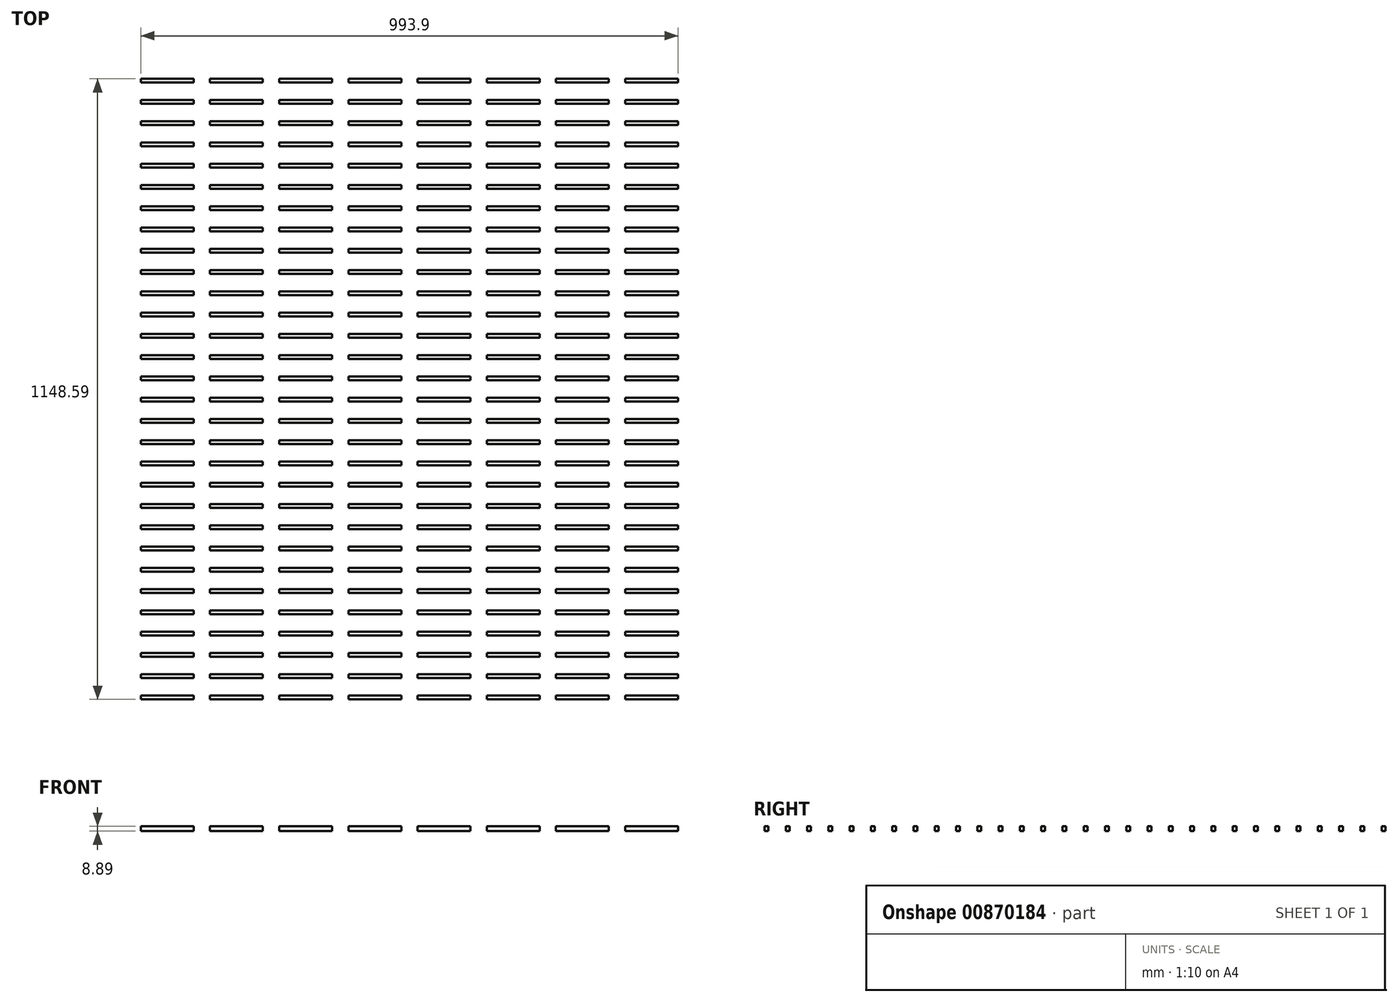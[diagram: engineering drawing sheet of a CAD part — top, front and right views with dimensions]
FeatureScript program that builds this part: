
annotation { "Feature Type Name" : "Feature", "Feature Type Description" : "" }
export const myFeature = defineFeature(function(context is Context, id is Id, definition is map)
    precondition{}
    {
        {
            var Q0;
            Q0=qCreatedBy(makeId("Top.planeOp"),FACE);
            var sketch = newSketch(context, id + "F0", { "sketchPlane" : qUnion([Q0])});
            skLineSegment(sketch, "E0.bottom", {"start": v(-104.49, 66.32) * mm, "end": v(-6.7, 66.32) * mm});
            skLineSegment(sketch, "E0.top", {"start": v(-104.49, 59.46) * mm, "end": v(-6.7, 59.46) * mm});
            skLineSegment(sketch, "E0.left", {"start": v(-104.49, 66.32) * mm, "end": v(-104.49, 59.46) * mm});
            skLineSegment(sketch, "E0.right", {"start": v(-6.7, 66.32) * mm, "end": v(-6.7, 59.46) * mm});
            skLineSegment(sketch, "E1.0.1.0", {"start": v(-104.49, 105.69) * mm, "end": v(-6.7, 105.69) * mm});
            skLineSegment(sketch, "E1.0.1.1", {"start": v(-104.49, 98.83) * mm, "end": v(-6.7, 98.83) * mm});
            skLineSegment(sketch, "E1.0.1.2", {"start": v(-6.7, 105.69) * mm, "end": v(-6.7, 98.83) * mm});
            skLineSegment(sketch, "E1.0.1.3", {"start": v(-104.49, 105.69) * mm, "end": v(-104.49, 98.83) * mm});
            skLineSegment(sketch, "E1.0.2.0", {"start": v(-104.49, 145.06) * mm, "end": v(-6.7, 145.06) * mm});
            skLineSegment(sketch, "E1.0.2.1", {"start": v(-104.49, 138.2) * mm, "end": v(-6.7, 138.2) * mm});
            skLineSegment(sketch, "E1.0.2.2", {"start": v(-6.7, 145.06) * mm, "end": v(-6.7, 138.2) * mm});
            skLineSegment(sketch, "E1.0.2.3", {"start": v(-104.49, 145.06) * mm, "end": v(-104.49, 138.2) * mm});
            skLineSegment(sketch, "E1.0.3.0", {"start": v(-104.49, 184.43) * mm, "end": v(-6.7, 184.43) * mm});
            skLineSegment(sketch, "E1.0.3.1", {"start": v(-104.49, 177.57) * mm, "end": v(-6.7, 177.57) * mm});
            skLineSegment(sketch, "E1.0.3.2", {"start": v(-6.7, 184.43) * mm, "end": v(-6.7, 177.57) * mm});
            skLineSegment(sketch, "E1.0.3.3", {"start": v(-104.49, 184.43) * mm, "end": v(-104.49, 177.57) * mm});
            skLineSegment(sketch, "E1.0.4.0", {"start": v(-104.49, 223.8) * mm, "end": v(-6.7, 223.8) * mm});
            skLineSegment(sketch, "E1.0.4.1", {"start": v(-104.49, 216.94) * mm, "end": v(-6.7, 216.94) * mm});
            skLineSegment(sketch, "E1.0.4.2", {"start": v(-6.7, 223.8) * mm, "end": v(-6.7, 216.94) * mm});
            skLineSegment(sketch, "E1.0.4.3", {"start": v(-104.49, 223.8) * mm, "end": v(-104.49, 216.94) * mm});
            skLineSegment(sketch, "E1.0.5.0", {"start": v(-104.49, 263.17) * mm, "end": v(-6.7, 263.17) * mm});
            skLineSegment(sketch, "E1.0.5.1", {"start": v(-104.49, 256.31) * mm, "end": v(-6.7, 256.31) * mm});
            skLineSegment(sketch, "E1.0.5.2", {"start": v(-6.7, 263.17) * mm, "end": v(-6.7, 256.31) * mm});
            skLineSegment(sketch, "E1.0.5.3", {"start": v(-104.49, 263.17) * mm, "end": v(-104.49, 256.31) * mm});
            skLineSegment(sketch, "E1.0.6.0", {"start": v(-104.49, 302.54) * mm, "end": v(-6.7, 302.54) * mm});
            skLineSegment(sketch, "E1.0.6.1", {"start": v(-104.49, 295.68) * mm, "end": v(-6.7, 295.68) * mm});
            skLineSegment(sketch, "E1.0.6.2", {"start": v(-6.7, 302.54) * mm, "end": v(-6.7, 295.68) * mm});
            skLineSegment(sketch, "E1.0.6.3", {"start": v(-104.49, 302.54) * mm, "end": v(-104.49, 295.68) * mm});
            skLineSegment(sketch, "E1.0.7.0", {"start": v(-104.49, 341.9) * mm, "end": v(-6.7, 341.9) * mm});
            skLineSegment(sketch, "E1.0.7.1", {"start": v(-104.49, 335.05) * mm, "end": v(-6.7, 335.05) * mm});
            skLineSegment(sketch, "E1.0.7.2", {"start": v(-6.7, 341.9) * mm, "end": v(-6.7, 335.05) * mm});
            skLineSegment(sketch, "E1.0.7.3", {"start": v(-104.49, 341.9) * mm, "end": v(-104.49, 335.05) * mm});
            skLineSegment(sketch, "E1.0.8.0", {"start": v(-104.49, 381.28) * mm, "end": v(-6.7, 381.28) * mm});
            skLineSegment(sketch, "E1.0.8.1", {"start": v(-104.49, 374.42) * mm, "end": v(-6.7, 374.42) * mm});
            skLineSegment(sketch, "E1.0.8.2", {"start": v(-6.7, 381.28) * mm, "end": v(-6.7, 374.42) * mm});
            skLineSegment(sketch, "E1.0.8.3", {"start": v(-104.49, 381.28) * mm, "end": v(-104.49, 374.42) * mm});
            skLineSegment(sketch, "E1.0.9.0", {"start": v(-104.49, 420.65) * mm, "end": v(-6.7, 420.65) * mm});
            skLineSegment(sketch, "E1.0.9.1", {"start": v(-104.49, 413.8) * mm, "end": v(-6.7, 413.8) * mm});
            skLineSegment(sketch, "E1.0.9.2", {"start": v(-6.7, 420.65) * mm, "end": v(-6.7, 413.8) * mm});
            skLineSegment(sketch, "E1.0.9.3", {"start": v(-104.49, 420.65) * mm, "end": v(-104.49, 413.8) * mm});
            skLineSegment(sketch, "E1.0.10.0", {"start": v(-104.49, 460.02) * mm, "end": v(-6.7, 460.02) * mm});
            skLineSegment(sketch, "E1.0.10.1", {"start": v(-104.49, 453.16) * mm, "end": v(-6.7, 453.16) * mm});
            skLineSegment(sketch, "E1.0.10.2", {"start": v(-6.7, 460.02) * mm, "end": v(-6.7, 453.16) * mm});
            skLineSegment(sketch, "E1.0.10.3", {"start": v(-104.49, 460.02) * mm, "end": v(-104.49, 453.16) * mm});
            skLineSegment(sketch, "E1.0.11.0", {"start": v(-104.49, 499.39) * mm, "end": v(-6.7, 499.39) * mm});
            skLineSegment(sketch, "E1.0.11.1", {"start": v(-104.49, 492.53) * mm, "end": v(-6.7, 492.53) * mm});
            skLineSegment(sketch, "E1.0.11.2", {"start": v(-6.7, 499.39) * mm, "end": v(-6.7, 492.53) * mm});
            skLineSegment(sketch, "E1.0.11.3", {"start": v(-104.49, 499.39) * mm, "end": v(-104.49, 492.53) * mm});
            skLineSegment(sketch, "E1.0.12.0", {"start": v(-104.49, 538.76) * mm, "end": v(-6.7, 538.76) * mm});
            skLineSegment(sketch, "E1.0.12.1", {"start": v(-104.49, 531.9) * mm, "end": v(-6.7, 531.9) * mm});
            skLineSegment(sketch, "E1.0.12.2", {"start": v(-6.7, 538.76) * mm, "end": v(-6.7, 531.9) * mm});
            skLineSegment(sketch, "E1.0.12.3", {"start": v(-104.49, 538.76) * mm, "end": v(-104.49, 531.9) * mm});
            skLineSegment(sketch, "E1.0.13.0", {"start": v(-104.49, 578.13) * mm, "end": v(-6.7, 578.13) * mm});
            skLineSegment(sketch, "E1.0.13.1", {"start": v(-104.49, 571.27) * mm, "end": v(-6.7, 571.27) * mm});
            skLineSegment(sketch, "E1.0.13.2", {"start": v(-6.7, 578.13) * mm, "end": v(-6.7, 571.27) * mm});
            skLineSegment(sketch, "E1.0.13.3", {"start": v(-104.49, 578.13) * mm, "end": v(-104.49, 571.27) * mm});
            skLineSegment(sketch, "E1.0.14.0", {"start": v(-104.49, 617.5) * mm, "end": v(-6.7, 617.5) * mm});
            skLineSegment(sketch, "E1.0.14.1", {"start": v(-104.49, 610.64) * mm, "end": v(-6.7, 610.64) * mm});
            skLineSegment(sketch, "E1.0.14.2", {"start": v(-6.7, 617.5) * mm, "end": v(-6.7, 610.64) * mm});
            skLineSegment(sketch, "E1.0.14.3", {"start": v(-104.49, 617.5) * mm, "end": v(-104.49, 610.64) * mm});
            skLineSegment(sketch, "E1.0.15.0", {"start": v(-104.49, 656.87) * mm, "end": v(-6.7, 656.87) * mm});
            skLineSegment(sketch, "E1.0.15.1", {"start": v(-104.49, 650.01) * mm, "end": v(-6.7, 650.01) * mm});
            skLineSegment(sketch, "E1.0.15.2", {"start": v(-6.7, 656.87) * mm, "end": v(-6.7, 650.01) * mm});
            skLineSegment(sketch, "E1.0.15.3", {"start": v(-104.49, 656.87) * mm, "end": v(-104.49, 650.01) * mm});
            skLineSegment(sketch, "E1.0.16.0", {"start": v(-104.49, 696.24) * mm, "end": v(-6.7, 696.24) * mm});
            skLineSegment(sketch, "E1.0.16.1", {"start": v(-104.49, 689.38) * mm, "end": v(-6.7, 689.38) * mm});
            skLineSegment(sketch, "E1.0.16.2", {"start": v(-6.7, 696.24) * mm, "end": v(-6.7, 689.38) * mm});
            skLineSegment(sketch, "E1.0.16.3", {"start": v(-104.49, 696.24) * mm, "end": v(-104.49, 689.38) * mm});
            skLineSegment(sketch, "E1.0.17.0", {"start": v(-104.49, 735.6) * mm, "end": v(-6.7, 735.6) * mm});
            skLineSegment(sketch, "E1.0.17.1", {"start": v(-104.49, 728.75) * mm, "end": v(-6.7, 728.75) * mm});
            skLineSegment(sketch, "E1.0.17.2", {"start": v(-6.7, 735.6) * mm, "end": v(-6.7, 728.75) * mm});
            skLineSegment(sketch, "E1.0.17.3", {"start": v(-104.49, 735.6) * mm, "end": v(-104.49, 728.75) * mm});
            skLineSegment(sketch, "E1.0.18.0", {"start": v(-104.49, 774.98) * mm, "end": v(-6.7, 774.98) * mm});
            skLineSegment(sketch, "E1.0.18.1", {"start": v(-104.49, 768.12) * mm, "end": v(-6.7, 768.12) * mm});
            skLineSegment(sketch, "E1.0.18.2", {"start": v(-6.7, 774.98) * mm, "end": v(-6.7, 768.12) * mm});
            skLineSegment(sketch, "E1.0.18.3", {"start": v(-104.49, 774.98) * mm, "end": v(-104.49, 768.12) * mm});
            skLineSegment(sketch, "E1.0.19.0", {"start": v(-104.49, 814.35) * mm, "end": v(-6.7, 814.35) * mm});
            skLineSegment(sketch, "E1.0.19.1", {"start": v(-104.49, 807.5) * mm, "end": v(-6.7, 807.5) * mm});
            skLineSegment(sketch, "E1.0.19.2", {"start": v(-6.7, 814.35) * mm, "end": v(-6.7, 807.5) * mm});
            skLineSegment(sketch, "E1.0.19.3", {"start": v(-104.49, 814.35) * mm, "end": v(-104.49, 807.5) * mm});
            skLineSegment(sketch, "E1.0.20.0", {"start": v(-104.49, 853.72) * mm, "end": v(-6.7, 853.72) * mm});
            skLineSegment(sketch, "E1.0.20.1", {"start": v(-104.49, 846.86) * mm, "end": v(-6.7, 846.86) * mm});
            skLineSegment(sketch, "E1.0.20.2", {"start": v(-6.7, 853.72) * mm, "end": v(-6.7, 846.86) * mm});
            skLineSegment(sketch, "E1.0.20.3", {"start": v(-104.49, 853.72) * mm, "end": v(-104.49, 846.86) * mm});
            skLineSegment(sketch, "E1.0.21.0", {"start": v(-104.49, 893.09) * mm, "end": v(-6.7, 893.09) * mm});
            skLineSegment(sketch, "E1.0.21.1", {"start": v(-104.49, 886.23) * mm, "end": v(-6.7, 886.23) * mm});
            skLineSegment(sketch, "E1.0.21.2", {"start": v(-6.7, 893.09) * mm, "end": v(-6.7, 886.23) * mm});
            skLineSegment(sketch, "E1.0.21.3", {"start": v(-104.49, 893.09) * mm, "end": v(-104.49, 886.23) * mm});
            skLineSegment(sketch, "E1.0.22.0", {"start": v(-104.49, 932.46) * mm, "end": v(-6.7, 932.46) * mm});
            skLineSegment(sketch, "E1.0.22.1", {"start": v(-104.49, 925.6) * mm, "end": v(-6.7, 925.6) * mm});
            skLineSegment(sketch, "E1.0.22.2", {"start": v(-6.7, 932.46) * mm, "end": v(-6.7, 925.6) * mm});
            skLineSegment(sketch, "E1.0.22.3", {"start": v(-104.49, 932.46) * mm, "end": v(-104.49, 925.6) * mm});
            skLineSegment(sketch, "E1.0.23.0", {"start": v(-104.49, 971.83) * mm, "end": v(-6.7, 971.83) * mm});
            skLineSegment(sketch, "E1.0.23.1", {"start": v(-104.49, 964.97) * mm, "end": v(-6.7, 964.97) * mm});
            skLineSegment(sketch, "E1.0.23.2", {"start": v(-6.7, 971.83) * mm, "end": v(-6.7, 964.97) * mm});
            skLineSegment(sketch, "E1.0.23.3", {"start": v(-104.49, 971.83) * mm, "end": v(-104.49, 964.97) * mm});
            skLineSegment(sketch, "E1.0.24.0", {"start": v(-104.49, 1011.2) * mm, "end": v(-6.7, 1011.2) * mm});
            skLineSegment(sketch, "E1.0.24.1", {"start": v(-104.49, 1004.34) * mm, "end": v(-6.7, 1004.34) * mm});
            skLineSegment(sketch, "E1.0.24.2", {"start": v(-6.7, 1011.2) * mm, "end": v(-6.7, 1004.34) * mm});
            skLineSegment(sketch, "E1.0.24.3", {"start": v(-104.49, 1011.2) * mm, "end": v(-104.49, 1004.34) * mm});
            skLineSegment(sketch, "E1.0.25.0", {"start": v(-104.49, 1050.57) * mm, "end": v(-6.7, 1050.57) * mm});
            skLineSegment(sketch, "E1.0.25.1", {"start": v(-104.49, 1043.71) * mm, "end": v(-6.7, 1043.71) * mm});
            skLineSegment(sketch, "E1.0.25.2", {"start": v(-6.7, 1050.57) * mm, "end": v(-6.7, 1043.71) * mm});
            skLineSegment(sketch, "E1.0.25.3", {"start": v(-104.49, 1050.57) * mm, "end": v(-104.49, 1043.71) * mm});
            skLineSegment(sketch, "E1.0.26.0", {"start": v(-104.49, 1089.94) * mm, "end": v(-6.7, 1089.94) * mm});
            skLineSegment(sketch, "E1.0.26.1", {"start": v(-104.49, 1083.08) * mm, "end": v(-6.7, 1083.08) * mm});
            skLineSegment(sketch, "E1.0.26.2", {"start": v(-6.7, 1089.94) * mm, "end": v(-6.7, 1083.08) * mm});
            skLineSegment(sketch, "E1.0.26.3", {"start": v(-104.49, 1089.94) * mm, "end": v(-104.49, 1083.08) * mm});
            skLineSegment(sketch, "E1.0.27.0", {"start": v(-104.49, 1129.3) * mm, "end": v(-6.7, 1129.3) * mm});
            skLineSegment(sketch, "E1.0.27.1", {"start": v(-104.49, 1122.45) * mm, "end": v(-6.7, 1122.45) * mm});
            skLineSegment(sketch, "E1.0.27.2", {"start": v(-6.7, 1129.3) * mm, "end": v(-6.7, 1122.45) * mm});
            skLineSegment(sketch, "E1.0.27.3", {"start": v(-104.49, 1129.3) * mm, "end": v(-104.49, 1122.45) * mm});
            skLineSegment(sketch, "E1.0.28.0", {"start": v(-104.49, 1168.68) * mm, "end": v(-6.7, 1168.68) * mm});
            skLineSegment(sketch, "E1.0.28.1", {"start": v(-104.49, 1161.82) * mm, "end": v(-6.7, 1161.82) * mm});
            skLineSegment(sketch, "E1.0.28.2", {"start": v(-6.7, 1168.68) * mm, "end": v(-6.7, 1161.82) * mm});
            skLineSegment(sketch, "E1.0.28.3", {"start": v(-104.49, 1168.68) * mm, "end": v(-104.49, 1161.82) * mm});
            skLineSegment(sketch, "E1.0.29.0", {"start": v(-104.49, 1208.05) * mm, "end": v(-6.7, 1208.05) * mm});
            skLineSegment(sketch, "E1.0.29.1", {"start": v(-104.49, 1201.2) * mm, "end": v(-6.7, 1201.2) * mm});
            skLineSegment(sketch, "E1.0.29.2", {"start": v(-6.7, 1208.05) * mm, "end": v(-6.7, 1201.2) * mm});
            skLineSegment(sketch, "E1.0.29.3", {"start": v(-104.49, 1208.05) * mm, "end": v(-104.49, 1201.2) * mm});
            skLineSegment(sketch, "E1.1.0.0", {"start": v(23.53, 66.32) * mm, "end": v(121.32, 66.32) * mm});
            skLineSegment(sketch, "E1.1.0.1", {"start": v(23.53, 59.46) * mm, "end": v(121.32, 59.46) * mm});
            skLineSegment(sketch, "E1.1.0.2", {"start": v(121.32, 66.32) * mm, "end": v(121.32, 59.46) * mm});
            skLineSegment(sketch, "E1.1.0.3", {"start": v(23.53, 66.32) * mm, "end": v(23.53, 59.46) * mm});
            skLineSegment(sketch, "E1.1.1.0", {"start": v(23.53, 105.69) * mm, "end": v(121.32, 105.69) * mm});
            skLineSegment(sketch, "E1.1.1.1", {"start": v(23.53, 98.83) * mm, "end": v(121.32, 98.83) * mm});
            skLineSegment(sketch, "E1.1.1.2", {"start": v(121.32, 105.69) * mm, "end": v(121.32, 98.83) * mm});
            skLineSegment(sketch, "E1.1.1.3", {"start": v(23.53, 105.69) * mm, "end": v(23.53, 98.83) * mm});
            skLineSegment(sketch, "E1.1.2.0", {"start": v(23.53, 145.06) * mm, "end": v(121.32, 145.06) * mm});
            skLineSegment(sketch, "E1.1.2.1", {"start": v(23.53, 138.2) * mm, "end": v(121.32, 138.2) * mm});
            skLineSegment(sketch, "E1.1.2.2", {"start": v(121.32, 145.06) * mm, "end": v(121.32, 138.2) * mm});
            skLineSegment(sketch, "E1.1.2.3", {"start": v(23.53, 145.06) * mm, "end": v(23.53, 138.2) * mm});
            skLineSegment(sketch, "E1.1.3.0", {"start": v(23.53, 184.43) * mm, "end": v(121.32, 184.43) * mm});
            skLineSegment(sketch, "E1.1.3.1", {"start": v(23.53, 177.57) * mm, "end": v(121.32, 177.57) * mm});
            skLineSegment(sketch, "E1.1.3.2", {"start": v(121.32, 184.43) * mm, "end": v(121.32, 177.57) * mm});
            skLineSegment(sketch, "E1.1.3.3", {"start": v(23.53, 184.43) * mm, "end": v(23.53, 177.57) * mm});
            skLineSegment(sketch, "E1.1.4.0", {"start": v(23.53, 223.8) * mm, "end": v(121.32, 223.8) * mm});
            skLineSegment(sketch, "E1.1.4.1", {"start": v(23.53, 216.94) * mm, "end": v(121.32, 216.94) * mm});
            skLineSegment(sketch, "E1.1.4.2", {"start": v(121.32, 223.8) * mm, "end": v(121.32, 216.94) * mm});
            skLineSegment(sketch, "E1.1.4.3", {"start": v(23.53, 223.8) * mm, "end": v(23.53, 216.94) * mm});
            skLineSegment(sketch, "E1.1.5.0", {"start": v(23.53, 263.17) * mm, "end": v(121.32, 263.17) * mm});
            skLineSegment(sketch, "E1.1.5.1", {"start": v(23.53, 256.31) * mm, "end": v(121.32, 256.31) * mm});
            skLineSegment(sketch, "E1.1.5.2", {"start": v(121.32, 263.17) * mm, "end": v(121.32, 256.31) * mm});
            skLineSegment(sketch, "E1.1.5.3", {"start": v(23.53, 263.17) * mm, "end": v(23.53, 256.31) * mm});
            skLineSegment(sketch, "E1.1.6.0", {"start": v(23.53, 302.54) * mm, "end": v(121.32, 302.54) * mm});
            skLineSegment(sketch, "E1.1.6.1", {"start": v(23.53, 295.68) * mm, "end": v(121.32, 295.68) * mm});
            skLineSegment(sketch, "E1.1.6.2", {"start": v(121.32, 302.54) * mm, "end": v(121.32, 295.68) * mm});
            skLineSegment(sketch, "E1.1.6.3", {"start": v(23.53, 302.54) * mm, "end": v(23.53, 295.68) * mm});
            skLineSegment(sketch, "E1.1.7.0", {"start": v(23.53, 341.9) * mm, "end": v(121.32, 341.9) * mm});
            skLineSegment(sketch, "E1.1.7.1", {"start": v(23.53, 335.05) * mm, "end": v(121.32, 335.05) * mm});
            skLineSegment(sketch, "E1.1.7.2", {"start": v(121.32, 341.9) * mm, "end": v(121.32, 335.05) * mm});
            skLineSegment(sketch, "E1.1.7.3", {"start": v(23.53, 341.9) * mm, "end": v(23.53, 335.05) * mm});
            skLineSegment(sketch, "E1.1.8.0", {"start": v(23.53, 381.28) * mm, "end": v(121.32, 381.28) * mm});
            skLineSegment(sketch, "E1.1.8.1", {"start": v(23.53, 374.42) * mm, "end": v(121.32, 374.42) * mm});
            skLineSegment(sketch, "E1.1.8.2", {"start": v(121.32, 381.28) * mm, "end": v(121.32, 374.42) * mm});
            skLineSegment(sketch, "E1.1.8.3", {"start": v(23.53, 381.28) * mm, "end": v(23.53, 374.42) * mm});
            skLineSegment(sketch, "E1.1.9.0", {"start": v(23.53, 420.65) * mm, "end": v(121.32, 420.65) * mm});
            skLineSegment(sketch, "E1.1.9.1", {"start": v(23.53, 413.8) * mm, "end": v(121.32, 413.8) * mm});
            skLineSegment(sketch, "E1.1.9.2", {"start": v(121.32, 420.65) * mm, "end": v(121.32, 413.8) * mm});
            skLineSegment(sketch, "E1.1.9.3", {"start": v(23.53, 420.65) * mm, "end": v(23.53, 413.8) * mm});
            skLineSegment(sketch, "E1.1.10.0", {"start": v(23.53, 460.02) * mm, "end": v(121.32, 460.02) * mm});
            skLineSegment(sketch, "E1.1.10.1", {"start": v(23.53, 453.16) * mm, "end": v(121.32, 453.16) * mm});
            skLineSegment(sketch, "E1.1.10.2", {"start": v(121.32, 460.02) * mm, "end": v(121.32, 453.16) * mm});
            skLineSegment(sketch, "E1.1.10.3", {"start": v(23.53, 460.02) * mm, "end": v(23.53, 453.16) * mm});
            skLineSegment(sketch, "E1.1.11.0", {"start": v(23.53, 499.39) * mm, "end": v(121.32, 499.39) * mm});
            skLineSegment(sketch, "E1.1.11.1", {"start": v(23.53, 492.53) * mm, "end": v(121.32, 492.53) * mm});
            skLineSegment(sketch, "E1.1.11.2", {"start": v(121.32, 499.39) * mm, "end": v(121.32, 492.53) * mm});
            skLineSegment(sketch, "E1.1.11.3", {"start": v(23.53, 499.39) * mm, "end": v(23.53, 492.53) * mm});
            skLineSegment(sketch, "E1.1.12.0", {"start": v(23.53, 538.76) * mm, "end": v(121.32, 538.76) * mm});
            skLineSegment(sketch, "E1.1.12.1", {"start": v(23.53, 531.9) * mm, "end": v(121.32, 531.9) * mm});
            skLineSegment(sketch, "E1.1.12.2", {"start": v(121.32, 538.76) * mm, "end": v(121.32, 531.9) * mm});
            skLineSegment(sketch, "E1.1.12.3", {"start": v(23.53, 538.76) * mm, "end": v(23.53, 531.9) * mm});
            skLineSegment(sketch, "E1.1.13.0", {"start": v(23.53, 578.13) * mm, "end": v(121.32, 578.13) * mm});
            skLineSegment(sketch, "E1.1.13.1", {"start": v(23.53, 571.27) * mm, "end": v(121.32, 571.27) * mm});
            skLineSegment(sketch, "E1.1.13.2", {"start": v(121.32, 578.13) * mm, "end": v(121.32, 571.27) * mm});
            skLineSegment(sketch, "E1.1.13.3", {"start": v(23.53, 578.13) * mm, "end": v(23.53, 571.27) * mm});
            skLineSegment(sketch, "E1.1.14.0", {"start": v(23.53, 617.5) * mm, "end": v(121.32, 617.5) * mm});
            skLineSegment(sketch, "E1.1.14.1", {"start": v(23.53, 610.64) * mm, "end": v(121.32, 610.64) * mm});
            skLineSegment(sketch, "E1.1.14.2", {"start": v(121.32, 617.5) * mm, "end": v(121.32, 610.64) * mm});
            skLineSegment(sketch, "E1.1.14.3", {"start": v(23.53, 617.5) * mm, "end": v(23.53, 610.64) * mm});
            skLineSegment(sketch, "E1.1.15.0", {"start": v(23.53, 656.87) * mm, "end": v(121.32, 656.87) * mm});
            skLineSegment(sketch, "E1.1.15.1", {"start": v(23.53, 650.01) * mm, "end": v(121.32, 650.01) * mm});
            skLineSegment(sketch, "E1.1.15.2", {"start": v(121.32, 656.87) * mm, "end": v(121.32, 650.01) * mm});
            skLineSegment(sketch, "E1.1.15.3", {"start": v(23.53, 656.87) * mm, "end": v(23.53, 650.01) * mm});
            skLineSegment(sketch, "E1.1.16.0", {"start": v(23.53, 696.24) * mm, "end": v(121.32, 696.24) * mm});
            skLineSegment(sketch, "E1.1.16.1", {"start": v(23.53, 689.38) * mm, "end": v(121.32, 689.38) * mm});
            skLineSegment(sketch, "E1.1.16.2", {"start": v(121.32, 696.24) * mm, "end": v(121.32, 689.38) * mm});
            skLineSegment(sketch, "E1.1.16.3", {"start": v(23.53, 696.24) * mm, "end": v(23.53, 689.38) * mm});
            skLineSegment(sketch, "E1.1.17.0", {"start": v(23.53, 735.6) * mm, "end": v(121.32, 735.6) * mm});
            skLineSegment(sketch, "E1.1.17.1", {"start": v(23.53, 728.75) * mm, "end": v(121.32, 728.75) * mm});
            skLineSegment(sketch, "E1.1.17.2", {"start": v(121.32, 735.6) * mm, "end": v(121.32, 728.75) * mm});
            skLineSegment(sketch, "E1.1.17.3", {"start": v(23.53, 735.6) * mm, "end": v(23.53, 728.75) * mm});
            skLineSegment(sketch, "E1.1.18.0", {"start": v(23.53, 774.98) * mm, "end": v(121.32, 774.98) * mm});
            skLineSegment(sketch, "E1.1.18.1", {"start": v(23.53, 768.12) * mm, "end": v(121.32, 768.12) * mm});
            skLineSegment(sketch, "E1.1.18.2", {"start": v(121.32, 774.98) * mm, "end": v(121.32, 768.12) * mm});
            skLineSegment(sketch, "E1.1.18.3", {"start": v(23.53, 774.98) * mm, "end": v(23.53, 768.12) * mm});
            skLineSegment(sketch, "E1.1.19.0", {"start": v(23.53, 814.35) * mm, "end": v(121.32, 814.35) * mm});
            skLineSegment(sketch, "E1.1.19.1", {"start": v(23.53, 807.5) * mm, "end": v(121.32, 807.5) * mm});
            skLineSegment(sketch, "E1.1.19.2", {"start": v(121.32, 814.35) * mm, "end": v(121.32, 807.5) * mm});
            skLineSegment(sketch, "E1.1.19.3", {"start": v(23.53, 814.35) * mm, "end": v(23.53, 807.5) * mm});
            skLineSegment(sketch, "E1.1.20.0", {"start": v(23.53, 853.72) * mm, "end": v(121.32, 853.72) * mm});
            skLineSegment(sketch, "E1.1.20.1", {"start": v(23.53, 846.86) * mm, "end": v(121.32, 846.86) * mm});
            skLineSegment(sketch, "E1.1.20.2", {"start": v(121.32, 853.72) * mm, "end": v(121.32, 846.86) * mm});
            skLineSegment(sketch, "E1.1.20.3", {"start": v(23.53, 853.72) * mm, "end": v(23.53, 846.86) * mm});
            skLineSegment(sketch, "E1.1.21.0", {"start": v(23.53, 893.09) * mm, "end": v(121.32, 893.09) * mm});
            skLineSegment(sketch, "E1.1.21.1", {"start": v(23.53, 886.23) * mm, "end": v(121.32, 886.23) * mm});
            skLineSegment(sketch, "E1.1.21.2", {"start": v(121.32, 893.09) * mm, "end": v(121.32, 886.23) * mm});
            skLineSegment(sketch, "E1.1.21.3", {"start": v(23.53, 893.09) * mm, "end": v(23.53, 886.23) * mm});
            skLineSegment(sketch, "E1.1.22.0", {"start": v(23.53, 932.46) * mm, "end": v(121.32, 932.46) * mm});
            skLineSegment(sketch, "E1.1.22.1", {"start": v(23.53, 925.6) * mm, "end": v(121.32, 925.6) * mm});
            skLineSegment(sketch, "E1.1.22.2", {"start": v(121.32, 932.46) * mm, "end": v(121.32, 925.6) * mm});
            skLineSegment(sketch, "E1.1.22.3", {"start": v(23.53, 932.46) * mm, "end": v(23.53, 925.6) * mm});
            skLineSegment(sketch, "E1.1.23.0", {"start": v(23.53, 971.83) * mm, "end": v(121.32, 971.83) * mm});
            skLineSegment(sketch, "E1.1.23.1", {"start": v(23.53, 964.97) * mm, "end": v(121.32, 964.97) * mm});
            skLineSegment(sketch, "E1.1.23.2", {"start": v(121.32, 971.83) * mm, "end": v(121.32, 964.97) * mm});
            skLineSegment(sketch, "E1.1.23.3", {"start": v(23.53, 971.83) * mm, "end": v(23.53, 964.97) * mm});
            skLineSegment(sketch, "E1.1.24.0", {"start": v(23.53, 1011.2) * mm, "end": v(121.32, 1011.2) * mm});
            skLineSegment(sketch, "E1.1.24.1", {"start": v(23.53, 1004.34) * mm, "end": v(121.32, 1004.34) * mm});
            skLineSegment(sketch, "E1.1.24.2", {"start": v(121.32, 1011.2) * mm, "end": v(121.32, 1004.34) * mm});
            skLineSegment(sketch, "E1.1.24.3", {"start": v(23.53, 1011.2) * mm, "end": v(23.53, 1004.34) * mm});
            skLineSegment(sketch, "E1.1.25.0", {"start": v(23.53, 1050.57) * mm, "end": v(121.32, 1050.57) * mm});
            skLineSegment(sketch, "E1.1.25.1", {"start": v(23.53, 1043.71) * mm, "end": v(121.32, 1043.71) * mm});
            skLineSegment(sketch, "E1.1.25.2", {"start": v(121.32, 1050.57) * mm, "end": v(121.32, 1043.71) * mm});
            skLineSegment(sketch, "E1.1.25.3", {"start": v(23.53, 1050.57) * mm, "end": v(23.53, 1043.71) * mm});
            skLineSegment(sketch, "E1.1.26.0", {"start": v(23.53, 1089.94) * mm, "end": v(121.32, 1089.94) * mm});
            skLineSegment(sketch, "E1.1.26.1", {"start": v(23.53, 1083.08) * mm, "end": v(121.32, 1083.08) * mm});
            skLineSegment(sketch, "E1.1.26.2", {"start": v(121.32, 1089.94) * mm, "end": v(121.32, 1083.08) * mm});
            skLineSegment(sketch, "E1.1.26.3", {"start": v(23.53, 1089.94) * mm, "end": v(23.53, 1083.08) * mm});
            skLineSegment(sketch, "E1.1.27.0", {"start": v(23.53, 1129.3) * mm, "end": v(121.32, 1129.3) * mm});
            skLineSegment(sketch, "E1.1.27.1", {"start": v(23.53, 1122.45) * mm, "end": v(121.32, 1122.45) * mm});
            skLineSegment(sketch, "E1.1.27.2", {"start": v(121.32, 1129.3) * mm, "end": v(121.32, 1122.45) * mm});
            skLineSegment(sketch, "E1.1.27.3", {"start": v(23.53, 1129.3) * mm, "end": v(23.53, 1122.45) * mm});
            skLineSegment(sketch, "E1.1.28.0", {"start": v(23.53, 1168.68) * mm, "end": v(121.32, 1168.68) * mm});
            skLineSegment(sketch, "E1.1.28.1", {"start": v(23.53, 1161.82) * mm, "end": v(121.32, 1161.82) * mm});
            skLineSegment(sketch, "E1.1.28.2", {"start": v(121.32, 1168.68) * mm, "end": v(121.32, 1161.82) * mm});
            skLineSegment(sketch, "E1.1.28.3", {"start": v(23.53, 1168.68) * mm, "end": v(23.53, 1161.82) * mm});
            skLineSegment(sketch, "E1.1.29.0", {"start": v(23.53, 1208.05) * mm, "end": v(121.32, 1208.05) * mm});
            skLineSegment(sketch, "E1.1.29.1", {"start": v(23.53, 1201.2) * mm, "end": v(121.32, 1201.2) * mm});
            skLineSegment(sketch, "E1.1.29.2", {"start": v(121.32, 1208.05) * mm, "end": v(121.32, 1201.2) * mm});
            skLineSegment(sketch, "E1.1.29.3", {"start": v(23.53, 1208.05) * mm, "end": v(23.53, 1201.2) * mm});
            skLineSegment(sketch, "E1.2.0.0", {"start": v(151.54, 66.32) * mm, "end": v(249.33, 66.32) * mm});
            skLineSegment(sketch, "E1.2.0.1", {"start": v(151.54, 59.46) * mm, "end": v(249.33, 59.46) * mm});
            skLineSegment(sketch, "E1.2.0.2", {"start": v(249.33, 66.32) * mm, "end": v(249.33, 59.46) * mm});
            skLineSegment(sketch, "E1.2.0.3", {"start": v(151.54, 66.32) * mm, "end": v(151.54, 59.46) * mm});
            skLineSegment(sketch, "E1.2.1.0", {"start": v(151.54, 105.69) * mm, "end": v(249.33, 105.69) * mm});
            skLineSegment(sketch, "E1.2.1.1", {"start": v(151.54, 98.83) * mm, "end": v(249.33, 98.83) * mm});
            skLineSegment(sketch, "E1.2.1.2", {"start": v(249.33, 105.69) * mm, "end": v(249.33, 98.83) * mm});
            skLineSegment(sketch, "E1.2.1.3", {"start": v(151.54, 105.69) * mm, "end": v(151.54, 98.83) * mm});
            skLineSegment(sketch, "E1.2.2.0", {"start": v(151.54, 145.06) * mm, "end": v(249.33, 145.06) * mm});
            skLineSegment(sketch, "E1.2.2.1", {"start": v(151.54, 138.2) * mm, "end": v(249.33, 138.2) * mm});
            skLineSegment(sketch, "E1.2.2.2", {"start": v(249.33, 145.06) * mm, "end": v(249.33, 138.2) * mm});
            skLineSegment(sketch, "E1.2.2.3", {"start": v(151.54, 145.06) * mm, "end": v(151.54, 138.2) * mm});
            skLineSegment(sketch, "E1.2.3.0", {"start": v(151.54, 184.43) * mm, "end": v(249.33, 184.43) * mm});
            skLineSegment(sketch, "E1.2.3.1", {"start": v(151.54, 177.57) * mm, "end": v(249.33, 177.57) * mm});
            skLineSegment(sketch, "E1.2.3.2", {"start": v(249.33, 184.43) * mm, "end": v(249.33, 177.57) * mm});
            skLineSegment(sketch, "E1.2.3.3", {"start": v(151.54, 184.43) * mm, "end": v(151.54, 177.57) * mm});
            skLineSegment(sketch, "E1.2.4.0", {"start": v(151.54, 223.8) * mm, "end": v(249.33, 223.8) * mm});
            skLineSegment(sketch, "E1.2.4.1", {"start": v(151.54, 216.94) * mm, "end": v(249.33, 216.94) * mm});
            skLineSegment(sketch, "E1.2.4.2", {"start": v(249.33, 223.8) * mm, "end": v(249.33, 216.94) * mm});
            skLineSegment(sketch, "E1.2.4.3", {"start": v(151.54, 223.8) * mm, "end": v(151.54, 216.94) * mm});
            skLineSegment(sketch, "E1.2.5.0", {"start": v(151.54, 263.17) * mm, "end": v(249.33, 263.17) * mm});
            skLineSegment(sketch, "E1.2.5.1", {"start": v(151.54, 256.31) * mm, "end": v(249.33, 256.31) * mm});
            skLineSegment(sketch, "E1.2.5.2", {"start": v(249.33, 263.17) * mm, "end": v(249.33, 256.31) * mm});
            skLineSegment(sketch, "E1.2.5.3", {"start": v(151.54, 263.17) * mm, "end": v(151.54, 256.31) * mm});
            skLineSegment(sketch, "E1.2.6.0", {"start": v(151.54, 302.54) * mm, "end": v(249.33, 302.54) * mm});
            skLineSegment(sketch, "E1.2.6.1", {"start": v(151.54, 295.68) * mm, "end": v(249.33, 295.68) * mm});
            skLineSegment(sketch, "E1.2.6.2", {"start": v(249.33, 302.54) * mm, "end": v(249.33, 295.68) * mm});
            skLineSegment(sketch, "E1.2.6.3", {"start": v(151.54, 302.54) * mm, "end": v(151.54, 295.68) * mm});
            skLineSegment(sketch, "E1.2.7.0", {"start": v(151.54, 341.9) * mm, "end": v(249.33, 341.9) * mm});
            skLineSegment(sketch, "E1.2.7.1", {"start": v(151.54, 335.05) * mm, "end": v(249.33, 335.05) * mm});
            skLineSegment(sketch, "E1.2.7.2", {"start": v(249.33, 341.9) * mm, "end": v(249.33, 335.05) * mm});
            skLineSegment(sketch, "E1.2.7.3", {"start": v(151.54, 341.9) * mm, "end": v(151.54, 335.05) * mm});
            skLineSegment(sketch, "E1.2.8.0", {"start": v(151.54, 381.28) * mm, "end": v(249.33, 381.28) * mm});
            skLineSegment(sketch, "E1.2.8.1", {"start": v(151.54, 374.42) * mm, "end": v(249.33, 374.42) * mm});
            skLineSegment(sketch, "E1.2.8.2", {"start": v(249.33, 381.28) * mm, "end": v(249.33, 374.42) * mm});
            skLineSegment(sketch, "E1.2.8.3", {"start": v(151.54, 381.28) * mm, "end": v(151.54, 374.42) * mm});
            skLineSegment(sketch, "E1.2.9.0", {"start": v(151.54, 420.65) * mm, "end": v(249.33, 420.65) * mm});
            skLineSegment(sketch, "E1.2.9.1", {"start": v(151.54, 413.8) * mm, "end": v(249.33, 413.8) * mm});
            skLineSegment(sketch, "E1.2.9.2", {"start": v(249.33, 420.65) * mm, "end": v(249.33, 413.8) * mm});
            skLineSegment(sketch, "E1.2.9.3", {"start": v(151.54, 420.65) * mm, "end": v(151.54, 413.8) * mm});
            skLineSegment(sketch, "E1.2.10.0", {"start": v(151.54, 460.02) * mm, "end": v(249.33, 460.02) * mm});
            skLineSegment(sketch, "E1.2.10.1", {"start": v(151.54, 453.16) * mm, "end": v(249.33, 453.16) * mm});
            skLineSegment(sketch, "E1.2.10.2", {"start": v(249.33, 460.02) * mm, "end": v(249.33, 453.16) * mm});
            skLineSegment(sketch, "E1.2.10.3", {"start": v(151.54, 460.02) * mm, "end": v(151.54, 453.16) * mm});
            skLineSegment(sketch, "E1.2.11.0", {"start": v(151.54, 499.39) * mm, "end": v(249.33, 499.39) * mm});
            skLineSegment(sketch, "E1.2.11.1", {"start": v(151.54, 492.53) * mm, "end": v(249.33, 492.53) * mm});
            skLineSegment(sketch, "E1.2.11.2", {"start": v(249.33, 499.39) * mm, "end": v(249.33, 492.53) * mm});
            skLineSegment(sketch, "E1.2.11.3", {"start": v(151.54, 499.39) * mm, "end": v(151.54, 492.53) * mm});
            skLineSegment(sketch, "E1.2.12.0", {"start": v(151.54, 538.76) * mm, "end": v(249.33, 538.76) * mm});
            skLineSegment(sketch, "E1.2.12.1", {"start": v(151.54, 531.9) * mm, "end": v(249.33, 531.9) * mm});
            skLineSegment(sketch, "E1.2.12.2", {"start": v(249.33, 538.76) * mm, "end": v(249.33, 531.9) * mm});
            skLineSegment(sketch, "E1.2.12.3", {"start": v(151.54, 538.76) * mm, "end": v(151.54, 531.9) * mm});
            skLineSegment(sketch, "E1.2.13.0", {"start": v(151.54, 578.13) * mm, "end": v(249.33, 578.13) * mm});
            skLineSegment(sketch, "E1.2.13.1", {"start": v(151.54, 571.27) * mm, "end": v(249.33, 571.27) * mm});
            skLineSegment(sketch, "E1.2.13.2", {"start": v(249.33, 578.13) * mm, "end": v(249.33, 571.27) * mm});
            skLineSegment(sketch, "E1.2.13.3", {"start": v(151.54, 578.13) * mm, "end": v(151.54, 571.27) * mm});
            skLineSegment(sketch, "E1.2.14.0", {"start": v(151.54, 617.5) * mm, "end": v(249.33, 617.5) * mm});
            skLineSegment(sketch, "E1.2.14.1", {"start": v(151.54, 610.64) * mm, "end": v(249.33, 610.64) * mm});
            skLineSegment(sketch, "E1.2.14.2", {"start": v(249.33, 617.5) * mm, "end": v(249.33, 610.64) * mm});
            skLineSegment(sketch, "E1.2.14.3", {"start": v(151.54, 617.5) * mm, "end": v(151.54, 610.64) * mm});
            skLineSegment(sketch, "E1.2.15.0", {"start": v(151.54, 656.87) * mm, "end": v(249.33, 656.87) * mm});
            skLineSegment(sketch, "E1.2.15.1", {"start": v(151.54, 650.01) * mm, "end": v(249.33, 650.01) * mm});
            skLineSegment(sketch, "E1.2.15.2", {"start": v(249.33, 656.87) * mm, "end": v(249.33, 650.01) * mm});
            skLineSegment(sketch, "E1.2.15.3", {"start": v(151.54, 656.87) * mm, "end": v(151.54, 650.01) * mm});
            skLineSegment(sketch, "E1.2.16.0", {"start": v(151.54, 696.24) * mm, "end": v(249.33, 696.24) * mm});
            skLineSegment(sketch, "E1.2.16.1", {"start": v(151.54, 689.38) * mm, "end": v(249.33, 689.38) * mm});
            skLineSegment(sketch, "E1.2.16.2", {"start": v(249.33, 696.24) * mm, "end": v(249.33, 689.38) * mm});
            skLineSegment(sketch, "E1.2.16.3", {"start": v(151.54, 696.24) * mm, "end": v(151.54, 689.38) * mm});
            skLineSegment(sketch, "E1.2.17.0", {"start": v(151.54, 735.6) * mm, "end": v(249.33, 735.6) * mm});
            skLineSegment(sketch, "E1.2.17.1", {"start": v(151.54, 728.75) * mm, "end": v(249.33, 728.75) * mm});
            skLineSegment(sketch, "E1.2.17.2", {"start": v(249.33, 735.6) * mm, "end": v(249.33, 728.75) * mm});
            skLineSegment(sketch, "E1.2.17.3", {"start": v(151.54, 735.6) * mm, "end": v(151.54, 728.75) * mm});
            skLineSegment(sketch, "E1.2.18.0", {"start": v(151.54, 774.98) * mm, "end": v(249.33, 774.98) * mm});
            skLineSegment(sketch, "E1.2.18.1", {"start": v(151.54, 768.12) * mm, "end": v(249.33, 768.12) * mm});
            skLineSegment(sketch, "E1.2.18.2", {"start": v(249.33, 774.98) * mm, "end": v(249.33, 768.12) * mm});
            skLineSegment(sketch, "E1.2.18.3", {"start": v(151.54, 774.98) * mm, "end": v(151.54, 768.12) * mm});
            skLineSegment(sketch, "E1.2.19.0", {"start": v(151.54, 814.35) * mm, "end": v(249.33, 814.35) * mm});
            skLineSegment(sketch, "E1.2.19.1", {"start": v(151.54, 807.5) * mm, "end": v(249.33, 807.5) * mm});
            skLineSegment(sketch, "E1.2.19.2", {"start": v(249.33, 814.35) * mm, "end": v(249.33, 807.5) * mm});
            skLineSegment(sketch, "E1.2.19.3", {"start": v(151.54, 814.35) * mm, "end": v(151.54, 807.5) * mm});
            skLineSegment(sketch, "E1.2.20.0", {"start": v(151.54, 853.72) * mm, "end": v(249.33, 853.72) * mm});
            skLineSegment(sketch, "E1.2.20.1", {"start": v(151.54, 846.86) * mm, "end": v(249.33, 846.86) * mm});
            skLineSegment(sketch, "E1.2.20.2", {"start": v(249.33, 853.72) * mm, "end": v(249.33, 846.86) * mm});
            skLineSegment(sketch, "E1.2.20.3", {"start": v(151.54, 853.72) * mm, "end": v(151.54, 846.86) * mm});
            skLineSegment(sketch, "E1.2.21.0", {"start": v(151.54, 893.09) * mm, "end": v(249.33, 893.09) * mm});
            skLineSegment(sketch, "E1.2.21.1", {"start": v(151.54, 886.23) * mm, "end": v(249.33, 886.23) * mm});
            skLineSegment(sketch, "E1.2.21.2", {"start": v(249.33, 893.09) * mm, "end": v(249.33, 886.23) * mm});
            skLineSegment(sketch, "E1.2.21.3", {"start": v(151.54, 893.09) * mm, "end": v(151.54, 886.23) * mm});
            skLineSegment(sketch, "E1.2.22.0", {"start": v(151.54, 932.46) * mm, "end": v(249.33, 932.46) * mm});
            skLineSegment(sketch, "E1.2.22.1", {"start": v(151.54, 925.6) * mm, "end": v(249.33, 925.6) * mm});
            skLineSegment(sketch, "E1.2.22.2", {"start": v(249.33, 932.46) * mm, "end": v(249.33, 925.6) * mm});
            skLineSegment(sketch, "E1.2.22.3", {"start": v(151.54, 932.46) * mm, "end": v(151.54, 925.6) * mm});
            skLineSegment(sketch, "E1.2.23.0", {"start": v(151.54, 971.83) * mm, "end": v(249.33, 971.83) * mm});
            skLineSegment(sketch, "E1.2.23.1", {"start": v(151.54, 964.97) * mm, "end": v(249.33, 964.97) * mm});
            skLineSegment(sketch, "E1.2.23.2", {"start": v(249.33, 971.83) * mm, "end": v(249.33, 964.97) * mm});
            skLineSegment(sketch, "E1.2.23.3", {"start": v(151.54, 971.83) * mm, "end": v(151.54, 964.97) * mm});
            skLineSegment(sketch, "E1.2.24.0", {"start": v(151.54, 1011.2) * mm, "end": v(249.33, 1011.2) * mm});
            skLineSegment(sketch, "E1.2.24.1", {"start": v(151.54, 1004.34) * mm, "end": v(249.33, 1004.34) * mm});
            skLineSegment(sketch, "E1.2.24.2", {"start": v(249.33, 1011.2) * mm, "end": v(249.33, 1004.34) * mm});
            skLineSegment(sketch, "E1.2.24.3", {"start": v(151.54, 1011.2) * mm, "end": v(151.54, 1004.34) * mm});
            skLineSegment(sketch, "E1.2.25.0", {"start": v(151.54, 1050.57) * mm, "end": v(249.33, 1050.57) * mm});
            skLineSegment(sketch, "E1.2.25.1", {"start": v(151.54, 1043.71) * mm, "end": v(249.33, 1043.71) * mm});
            skLineSegment(sketch, "E1.2.25.2", {"start": v(249.33, 1050.57) * mm, "end": v(249.33, 1043.71) * mm});
            skLineSegment(sketch, "E1.2.25.3", {"start": v(151.54, 1050.57) * mm, "end": v(151.54, 1043.71) * mm});
            skLineSegment(sketch, "E1.2.26.0", {"start": v(151.54, 1089.94) * mm, "end": v(249.33, 1089.94) * mm});
            skLineSegment(sketch, "E1.2.26.1", {"start": v(151.54, 1083.08) * mm, "end": v(249.33, 1083.08) * mm});
            skLineSegment(sketch, "E1.2.26.2", {"start": v(249.33, 1089.94) * mm, "end": v(249.33, 1083.08) * mm});
            skLineSegment(sketch, "E1.2.26.3", {"start": v(151.54, 1089.94) * mm, "end": v(151.54, 1083.08) * mm});
            skLineSegment(sketch, "E1.2.27.0", {"start": v(151.54, 1129.3) * mm, "end": v(249.33, 1129.3) * mm});
            skLineSegment(sketch, "E1.2.27.1", {"start": v(151.54, 1122.45) * mm, "end": v(249.33, 1122.45) * mm});
            skLineSegment(sketch, "E1.2.27.2", {"start": v(249.33, 1129.3) * mm, "end": v(249.33, 1122.45) * mm});
            skLineSegment(sketch, "E1.2.27.3", {"start": v(151.54, 1129.3) * mm, "end": v(151.54, 1122.45) * mm});
            skLineSegment(sketch, "E1.2.28.0", {"start": v(151.54, 1168.68) * mm, "end": v(249.33, 1168.68) * mm});
            skLineSegment(sketch, "E1.2.28.1", {"start": v(151.54, 1161.82) * mm, "end": v(249.33, 1161.82) * mm});
            skLineSegment(sketch, "E1.2.28.2", {"start": v(249.33, 1168.68) * mm, "end": v(249.33, 1161.82) * mm});
            skLineSegment(sketch, "E1.2.28.3", {"start": v(151.54, 1168.68) * mm, "end": v(151.54, 1161.82) * mm});
            skLineSegment(sketch, "E1.2.29.0", {"start": v(151.54, 1208.05) * mm, "end": v(249.33, 1208.05) * mm});
            skLineSegment(sketch, "E1.2.29.1", {"start": v(151.54, 1201.2) * mm, "end": v(249.33, 1201.2) * mm});
            skLineSegment(sketch, "E1.2.29.2", {"start": v(249.33, 1208.05) * mm, "end": v(249.33, 1201.2) * mm});
            skLineSegment(sketch, "E1.2.29.3", {"start": v(151.54, 1208.05) * mm, "end": v(151.54, 1201.2) * mm});
            skLineSegment(sketch, "E1.3.0.0", {"start": v(279.56, 66.32) * mm, "end": v(377.35, 66.32) * mm});
            skLineSegment(sketch, "E1.3.0.1", {"start": v(279.56, 59.46) * mm, "end": v(377.35, 59.46) * mm});
            skLineSegment(sketch, "E1.3.0.2", {"start": v(377.35, 66.32) * mm, "end": v(377.35, 59.46) * mm});
            skLineSegment(sketch, "E1.3.0.3", {"start": v(279.56, 66.32) * mm, "end": v(279.56, 59.46) * mm});
            skLineSegment(sketch, "E1.3.1.0", {"start": v(279.56, 105.69) * mm, "end": v(377.35, 105.69) * mm});
            skLineSegment(sketch, "E1.3.1.1", {"start": v(279.56, 98.83) * mm, "end": v(377.35, 98.83) * mm});
            skLineSegment(sketch, "E1.3.1.2", {"start": v(377.35, 105.69) * mm, "end": v(377.35, 98.83) * mm});
            skLineSegment(sketch, "E1.3.1.3", {"start": v(279.56, 105.69) * mm, "end": v(279.56, 98.83) * mm});
            skLineSegment(sketch, "E1.3.2.0", {"start": v(279.56, 145.06) * mm, "end": v(377.35, 145.06) * mm});
            skLineSegment(sketch, "E1.3.2.1", {"start": v(279.56, 138.2) * mm, "end": v(377.35, 138.2) * mm});
            skLineSegment(sketch, "E1.3.2.2", {"start": v(377.35, 145.06) * mm, "end": v(377.35, 138.2) * mm});
            skLineSegment(sketch, "E1.3.2.3", {"start": v(279.56, 145.06) * mm, "end": v(279.56, 138.2) * mm});
            skLineSegment(sketch, "E1.3.3.0", {"start": v(279.56, 184.43) * mm, "end": v(377.35, 184.43) * mm});
            skLineSegment(sketch, "E1.3.3.1", {"start": v(279.56, 177.57) * mm, "end": v(377.35, 177.57) * mm});
            skLineSegment(sketch, "E1.3.3.2", {"start": v(377.35, 184.43) * mm, "end": v(377.35, 177.57) * mm});
            skLineSegment(sketch, "E1.3.3.3", {"start": v(279.56, 184.43) * mm, "end": v(279.56, 177.57) * mm});
            skLineSegment(sketch, "E1.3.4.0", {"start": v(279.56, 223.8) * mm, "end": v(377.35, 223.8) * mm});
            skLineSegment(sketch, "E1.3.4.1", {"start": v(279.56, 216.94) * mm, "end": v(377.35, 216.94) * mm});
            skLineSegment(sketch, "E1.3.4.2", {"start": v(377.35, 223.8) * mm, "end": v(377.35, 216.94) * mm});
            skLineSegment(sketch, "E1.3.4.3", {"start": v(279.56, 223.8) * mm, "end": v(279.56, 216.94) * mm});
            skLineSegment(sketch, "E1.3.5.0", {"start": v(279.56, 263.17) * mm, "end": v(377.35, 263.17) * mm});
            skLineSegment(sketch, "E1.3.5.1", {"start": v(279.56, 256.31) * mm, "end": v(377.35, 256.31) * mm});
            skLineSegment(sketch, "E1.3.5.2", {"start": v(377.35, 263.17) * mm, "end": v(377.35, 256.31) * mm});
            skLineSegment(sketch, "E1.3.5.3", {"start": v(279.56, 263.17) * mm, "end": v(279.56, 256.31) * mm});
            skLineSegment(sketch, "E1.3.6.0", {"start": v(279.56, 302.54) * mm, "end": v(377.35, 302.54) * mm});
            skLineSegment(sketch, "E1.3.6.1", {"start": v(279.56, 295.68) * mm, "end": v(377.35, 295.68) * mm});
            skLineSegment(sketch, "E1.3.6.2", {"start": v(377.35, 302.54) * mm, "end": v(377.35, 295.68) * mm});
            skLineSegment(sketch, "E1.3.6.3", {"start": v(279.56, 302.54) * mm, "end": v(279.56, 295.68) * mm});
            skLineSegment(sketch, "E1.3.7.0", {"start": v(279.56, 341.9) * mm, "end": v(377.35, 341.9) * mm});
            skLineSegment(sketch, "E1.3.7.1", {"start": v(279.56, 335.05) * mm, "end": v(377.35, 335.05) * mm});
            skLineSegment(sketch, "E1.3.7.2", {"start": v(377.35, 341.9) * mm, "end": v(377.35, 335.05) * mm});
            skLineSegment(sketch, "E1.3.7.3", {"start": v(279.56, 341.9) * mm, "end": v(279.56, 335.05) * mm});
            skLineSegment(sketch, "E1.3.8.0", {"start": v(279.56, 381.28) * mm, "end": v(377.35, 381.28) * mm});
            skLineSegment(sketch, "E1.3.8.1", {"start": v(279.56, 374.42) * mm, "end": v(377.35, 374.42) * mm});
            skLineSegment(sketch, "E1.3.8.2", {"start": v(377.35, 381.28) * mm, "end": v(377.35, 374.42) * mm});
            skLineSegment(sketch, "E1.3.8.3", {"start": v(279.56, 381.28) * mm, "end": v(279.56, 374.42) * mm});
            skLineSegment(sketch, "E1.3.9.0", {"start": v(279.56, 420.65) * mm, "end": v(377.35, 420.65) * mm});
            skLineSegment(sketch, "E1.3.9.1", {"start": v(279.56, 413.8) * mm, "end": v(377.35, 413.8) * mm});
            skLineSegment(sketch, "E1.3.9.2", {"start": v(377.35, 420.65) * mm, "end": v(377.35, 413.8) * mm});
            skLineSegment(sketch, "E1.3.9.3", {"start": v(279.56, 420.65) * mm, "end": v(279.56, 413.8) * mm});
            skLineSegment(sketch, "E1.3.10.0", {"start": v(279.56, 460.02) * mm, "end": v(377.35, 460.02) * mm});
            skLineSegment(sketch, "E1.3.10.1", {"start": v(279.56, 453.16) * mm, "end": v(377.35, 453.16) * mm});
            skLineSegment(sketch, "E1.3.10.2", {"start": v(377.35, 460.02) * mm, "end": v(377.35, 453.16) * mm});
            skLineSegment(sketch, "E1.3.10.3", {"start": v(279.56, 460.02) * mm, "end": v(279.56, 453.16) * mm});
            skLineSegment(sketch, "E1.3.11.0", {"start": v(279.56, 499.39) * mm, "end": v(377.35, 499.39) * mm});
            skLineSegment(sketch, "E1.3.11.1", {"start": v(279.56, 492.53) * mm, "end": v(377.35, 492.53) * mm});
            skLineSegment(sketch, "E1.3.11.2", {"start": v(377.35, 499.39) * mm, "end": v(377.35, 492.53) * mm});
            skLineSegment(sketch, "E1.3.11.3", {"start": v(279.56, 499.39) * mm, "end": v(279.56, 492.53) * mm});
            skLineSegment(sketch, "E1.3.12.0", {"start": v(279.56, 538.76) * mm, "end": v(377.35, 538.76) * mm});
            skLineSegment(sketch, "E1.3.12.1", {"start": v(279.56, 531.9) * mm, "end": v(377.35, 531.9) * mm});
            skLineSegment(sketch, "E1.3.12.2", {"start": v(377.35, 538.76) * mm, "end": v(377.35, 531.9) * mm});
            skLineSegment(sketch, "E1.3.12.3", {"start": v(279.56, 538.76) * mm, "end": v(279.56, 531.9) * mm});
            skLineSegment(sketch, "E1.3.13.0", {"start": v(279.56, 578.13) * mm, "end": v(377.35, 578.13) * mm});
            skLineSegment(sketch, "E1.3.13.1", {"start": v(279.56, 571.27) * mm, "end": v(377.35, 571.27) * mm});
            skLineSegment(sketch, "E1.3.13.2", {"start": v(377.35, 578.13) * mm, "end": v(377.35, 571.27) * mm});
            skLineSegment(sketch, "E1.3.13.3", {"start": v(279.56, 578.13) * mm, "end": v(279.56, 571.27) * mm});
            skLineSegment(sketch, "E1.3.14.0", {"start": v(279.56, 617.5) * mm, "end": v(377.35, 617.5) * mm});
            skLineSegment(sketch, "E1.3.14.1", {"start": v(279.56, 610.64) * mm, "end": v(377.35, 610.64) * mm});
            skLineSegment(sketch, "E1.3.14.2", {"start": v(377.35, 617.5) * mm, "end": v(377.35, 610.64) * mm});
            skLineSegment(sketch, "E1.3.14.3", {"start": v(279.56, 617.5) * mm, "end": v(279.56, 610.64) * mm});
            skLineSegment(sketch, "E1.3.15.0", {"start": v(279.56, 656.87) * mm, "end": v(377.35, 656.87) * mm});
            skLineSegment(sketch, "E1.3.15.1", {"start": v(279.56, 650.01) * mm, "end": v(377.35, 650.01) * mm});
            skLineSegment(sketch, "E1.3.15.2", {"start": v(377.35, 656.87) * mm, "end": v(377.35, 650.01) * mm});
            skLineSegment(sketch, "E1.3.15.3", {"start": v(279.56, 656.87) * mm, "end": v(279.56, 650.01) * mm});
            skLineSegment(sketch, "E1.3.16.0", {"start": v(279.56, 696.24) * mm, "end": v(377.35, 696.24) * mm});
            skLineSegment(sketch, "E1.3.16.1", {"start": v(279.56, 689.38) * mm, "end": v(377.35, 689.38) * mm});
            skLineSegment(sketch, "E1.3.16.2", {"start": v(377.35, 696.24) * mm, "end": v(377.35, 689.38) * mm});
            skLineSegment(sketch, "E1.3.16.3", {"start": v(279.56, 696.24) * mm, "end": v(279.56, 689.38) * mm});
            skLineSegment(sketch, "E1.3.17.0", {"start": v(279.56, 735.6) * mm, "end": v(377.35, 735.6) * mm});
            skLineSegment(sketch, "E1.3.17.1", {"start": v(279.56, 728.75) * mm, "end": v(377.35, 728.75) * mm});
            skLineSegment(sketch, "E1.3.17.2", {"start": v(377.35, 735.6) * mm, "end": v(377.35, 728.75) * mm});
            skLineSegment(sketch, "E1.3.17.3", {"start": v(279.56, 735.6) * mm, "end": v(279.56, 728.75) * mm});
            skLineSegment(sketch, "E1.3.18.0", {"start": v(279.56, 774.98) * mm, "end": v(377.35, 774.98) * mm});
            skLineSegment(sketch, "E1.3.18.1", {"start": v(279.56, 768.12) * mm, "end": v(377.35, 768.12) * mm});
            skLineSegment(sketch, "E1.3.18.2", {"start": v(377.35, 774.98) * mm, "end": v(377.35, 768.12) * mm});
            skLineSegment(sketch, "E1.3.18.3", {"start": v(279.56, 774.98) * mm, "end": v(279.56, 768.12) * mm});
            skLineSegment(sketch, "E1.3.19.0", {"start": v(279.56, 814.35) * mm, "end": v(377.35, 814.35) * mm});
            skLineSegment(sketch, "E1.3.19.1", {"start": v(279.56, 807.5) * mm, "end": v(377.35, 807.5) * mm});
            skLineSegment(sketch, "E1.3.19.2", {"start": v(377.35, 814.35) * mm, "end": v(377.35, 807.5) * mm});
            skLineSegment(sketch, "E1.3.19.3", {"start": v(279.56, 814.35) * mm, "end": v(279.56, 807.5) * mm});
            skLineSegment(sketch, "E1.3.20.0", {"start": v(279.56, 853.72) * mm, "end": v(377.35, 853.72) * mm});
            skLineSegment(sketch, "E1.3.20.1", {"start": v(279.56, 846.86) * mm, "end": v(377.35, 846.86) * mm});
            skLineSegment(sketch, "E1.3.20.2", {"start": v(377.35, 853.72) * mm, "end": v(377.35, 846.86) * mm});
            skLineSegment(sketch, "E1.3.20.3", {"start": v(279.56, 853.72) * mm, "end": v(279.56, 846.86) * mm});
            skLineSegment(sketch, "E1.3.21.0", {"start": v(279.56, 893.09) * mm, "end": v(377.35, 893.09) * mm});
            skLineSegment(sketch, "E1.3.21.1", {"start": v(279.56, 886.23) * mm, "end": v(377.35, 886.23) * mm});
            skLineSegment(sketch, "E1.3.21.2", {"start": v(377.35, 893.09) * mm, "end": v(377.35, 886.23) * mm});
            skLineSegment(sketch, "E1.3.21.3", {"start": v(279.56, 893.09) * mm, "end": v(279.56, 886.23) * mm});
            skLineSegment(sketch, "E1.3.22.0", {"start": v(279.56, 932.46) * mm, "end": v(377.35, 932.46) * mm});
            skLineSegment(sketch, "E1.3.22.1", {"start": v(279.56, 925.6) * mm, "end": v(377.35, 925.6) * mm});
            skLineSegment(sketch, "E1.3.22.2", {"start": v(377.35, 932.46) * mm, "end": v(377.35, 925.6) * mm});
            skLineSegment(sketch, "E1.3.22.3", {"start": v(279.56, 932.46) * mm, "end": v(279.56, 925.6) * mm});
            skLineSegment(sketch, "E1.3.23.0", {"start": v(279.56, 971.83) * mm, "end": v(377.35, 971.83) * mm});
            skLineSegment(sketch, "E1.3.23.1", {"start": v(279.56, 964.97) * mm, "end": v(377.35, 964.97) * mm});
            skLineSegment(sketch, "E1.3.23.2", {"start": v(377.35, 971.83) * mm, "end": v(377.35, 964.97) * mm});
            skLineSegment(sketch, "E1.3.23.3", {"start": v(279.56, 971.83) * mm, "end": v(279.56, 964.97) * mm});
            skLineSegment(sketch, "E1.3.24.0", {"start": v(279.56, 1011.2) * mm, "end": v(377.35, 1011.2) * mm});
            skLineSegment(sketch, "E1.3.24.1", {"start": v(279.56, 1004.34) * mm, "end": v(377.35, 1004.34) * mm});
            skLineSegment(sketch, "E1.3.24.2", {"start": v(377.35, 1011.2) * mm, "end": v(377.35, 1004.34) * mm});
            skLineSegment(sketch, "E1.3.24.3", {"start": v(279.56, 1011.2) * mm, "end": v(279.56, 1004.34) * mm});
            skLineSegment(sketch, "E1.3.25.0", {"start": v(279.56, 1050.57) * mm, "end": v(377.35, 1050.57) * mm});
            skLineSegment(sketch, "E1.3.25.1", {"start": v(279.56, 1043.71) * mm, "end": v(377.35, 1043.71) * mm});
            skLineSegment(sketch, "E1.3.25.2", {"start": v(377.35, 1050.57) * mm, "end": v(377.35, 1043.71) * mm});
            skLineSegment(sketch, "E1.3.25.3", {"start": v(279.56, 1050.57) * mm, "end": v(279.56, 1043.71) * mm});
            skLineSegment(sketch, "E1.3.26.0", {"start": v(279.56, 1089.94) * mm, "end": v(377.35, 1089.94) * mm});
            skLineSegment(sketch, "E1.3.26.1", {"start": v(279.56, 1083.08) * mm, "end": v(377.35, 1083.08) * mm});
            skLineSegment(sketch, "E1.3.26.2", {"start": v(377.35, 1089.94) * mm, "end": v(377.35, 1083.08) * mm});
            skLineSegment(sketch, "E1.3.26.3", {"start": v(279.56, 1089.94) * mm, "end": v(279.56, 1083.08) * mm});
            skLineSegment(sketch, "E1.3.27.0", {"start": v(279.56, 1129.3) * mm, "end": v(377.35, 1129.3) * mm});
            skLineSegment(sketch, "E1.3.27.1", {"start": v(279.56, 1122.45) * mm, "end": v(377.35, 1122.45) * mm});
            skLineSegment(sketch, "E1.3.27.2", {"start": v(377.35, 1129.3) * mm, "end": v(377.35, 1122.45) * mm});
            skLineSegment(sketch, "E1.3.27.3", {"start": v(279.56, 1129.3) * mm, "end": v(279.56, 1122.45) * mm});
            skLineSegment(sketch, "E1.3.28.0", {"start": v(279.56, 1168.68) * mm, "end": v(377.35, 1168.68) * mm});
            skLineSegment(sketch, "E1.3.28.1", {"start": v(279.56, 1161.82) * mm, "end": v(377.35, 1161.82) * mm});
            skLineSegment(sketch, "E1.3.28.2", {"start": v(377.35, 1168.68) * mm, "end": v(377.35, 1161.82) * mm});
            skLineSegment(sketch, "E1.3.28.3", {"start": v(279.56, 1168.68) * mm, "end": v(279.56, 1161.82) * mm});
            skLineSegment(sketch, "E1.3.29.0", {"start": v(279.56, 1208.05) * mm, "end": v(377.35, 1208.05) * mm});
            skLineSegment(sketch, "E1.3.29.1", {"start": v(279.56, 1201.2) * mm, "end": v(377.35, 1201.2) * mm});
            skLineSegment(sketch, "E1.3.29.2", {"start": v(377.35, 1208.05) * mm, "end": v(377.35, 1201.2) * mm});
            skLineSegment(sketch, "E1.3.29.3", {"start": v(279.56, 1208.05) * mm, "end": v(279.56, 1201.2) * mm});
            skLineSegment(sketch, "E1.4.0.0", {"start": v(407.57, 66.32) * mm, "end": v(505.36, 66.32) * mm});
            skLineSegment(sketch, "E1.4.0.1", {"start": v(407.57, 59.46) * mm, "end": v(505.36, 59.46) * mm});
            skLineSegment(sketch, "E1.4.0.2", {"start": v(505.36, 66.32) * mm, "end": v(505.36, 59.46) * mm});
            skLineSegment(sketch, "E1.4.0.3", {"start": v(407.57, 66.32) * mm, "end": v(407.57, 59.46) * mm});
            skLineSegment(sketch, "E1.4.1.0", {"start": v(407.57, 105.69) * mm, "end": v(505.36, 105.69) * mm});
            skLineSegment(sketch, "E1.4.1.1", {"start": v(407.57, 98.83) * mm, "end": v(505.36, 98.83) * mm});
            skLineSegment(sketch, "E1.4.1.2", {"start": v(505.36, 105.69) * mm, "end": v(505.36, 98.83) * mm});
            skLineSegment(sketch, "E1.4.1.3", {"start": v(407.57, 105.69) * mm, "end": v(407.57, 98.83) * mm});
            skLineSegment(sketch, "E1.4.2.0", {"start": v(407.57, 145.06) * mm, "end": v(505.36, 145.06) * mm});
            skLineSegment(sketch, "E1.4.2.1", {"start": v(407.57, 138.2) * mm, "end": v(505.36, 138.2) * mm});
            skLineSegment(sketch, "E1.4.2.2", {"start": v(505.36, 145.06) * mm, "end": v(505.36, 138.2) * mm});
            skLineSegment(sketch, "E1.4.2.3", {"start": v(407.57, 145.06) * mm, "end": v(407.57, 138.2) * mm});
            skLineSegment(sketch, "E1.4.3.0", {"start": v(407.57, 184.43) * mm, "end": v(505.36, 184.43) * mm});
            skLineSegment(sketch, "E1.4.3.1", {"start": v(407.57, 177.57) * mm, "end": v(505.36, 177.57) * mm});
            skLineSegment(sketch, "E1.4.3.2", {"start": v(505.36, 184.43) * mm, "end": v(505.36, 177.57) * mm});
            skLineSegment(sketch, "E1.4.3.3", {"start": v(407.57, 184.43) * mm, "end": v(407.57, 177.57) * mm});
            skLineSegment(sketch, "E1.4.4.0", {"start": v(407.57, 223.8) * mm, "end": v(505.36, 223.8) * mm});
            skLineSegment(sketch, "E1.4.4.1", {"start": v(407.57, 216.94) * mm, "end": v(505.36, 216.94) * mm});
            skLineSegment(sketch, "E1.4.4.2", {"start": v(505.36, 223.8) * mm, "end": v(505.36, 216.94) * mm});
            skLineSegment(sketch, "E1.4.4.3", {"start": v(407.57, 223.8) * mm, "end": v(407.57, 216.94) * mm});
            skLineSegment(sketch, "E1.4.5.0", {"start": v(407.57, 263.17) * mm, "end": v(505.36, 263.17) * mm});
            skLineSegment(sketch, "E1.4.5.1", {"start": v(407.57, 256.31) * mm, "end": v(505.36, 256.31) * mm});
            skLineSegment(sketch, "E1.4.5.2", {"start": v(505.36, 263.17) * mm, "end": v(505.36, 256.31) * mm});
            skLineSegment(sketch, "E1.4.5.3", {"start": v(407.57, 263.17) * mm, "end": v(407.57, 256.31) * mm});
            skLineSegment(sketch, "E1.4.6.0", {"start": v(407.57, 302.54) * mm, "end": v(505.36, 302.54) * mm});
            skLineSegment(sketch, "E1.4.6.1", {"start": v(407.57, 295.68) * mm, "end": v(505.36, 295.68) * mm});
            skLineSegment(sketch, "E1.4.6.2", {"start": v(505.36, 302.54) * mm, "end": v(505.36, 295.68) * mm});
            skLineSegment(sketch, "E1.4.6.3", {"start": v(407.57, 302.54) * mm, "end": v(407.57, 295.68) * mm});
            skLineSegment(sketch, "E1.4.7.0", {"start": v(407.57, 341.9) * mm, "end": v(505.36, 341.9) * mm});
            skLineSegment(sketch, "E1.4.7.1", {"start": v(407.57, 335.05) * mm, "end": v(505.36, 335.05) * mm});
            skLineSegment(sketch, "E1.4.7.2", {"start": v(505.36, 341.9) * mm, "end": v(505.36, 335.05) * mm});
            skLineSegment(sketch, "E1.4.7.3", {"start": v(407.57, 341.9) * mm, "end": v(407.57, 335.05) * mm});
            skLineSegment(sketch, "E1.4.8.0", {"start": v(407.57, 381.28) * mm, "end": v(505.36, 381.28) * mm});
            skLineSegment(sketch, "E1.4.8.1", {"start": v(407.57, 374.42) * mm, "end": v(505.36, 374.42) * mm});
            skLineSegment(sketch, "E1.4.8.2", {"start": v(505.36, 381.28) * mm, "end": v(505.36, 374.42) * mm});
            skLineSegment(sketch, "E1.4.8.3", {"start": v(407.57, 381.28) * mm, "end": v(407.57, 374.42) * mm});
            skLineSegment(sketch, "E1.4.9.0", {"start": v(407.57, 420.65) * mm, "end": v(505.36, 420.65) * mm});
            skLineSegment(sketch, "E1.4.9.1", {"start": v(407.57, 413.8) * mm, "end": v(505.36, 413.8) * mm});
            skLineSegment(sketch, "E1.4.9.2", {"start": v(505.36, 420.65) * mm, "end": v(505.36, 413.8) * mm});
            skLineSegment(sketch, "E1.4.9.3", {"start": v(407.57, 420.65) * mm, "end": v(407.57, 413.8) * mm});
            skLineSegment(sketch, "E1.4.10.0", {"start": v(407.57, 460.02) * mm, "end": v(505.36, 460.02) * mm});
            skLineSegment(sketch, "E1.4.10.1", {"start": v(407.57, 453.16) * mm, "end": v(505.36, 453.16) * mm});
            skLineSegment(sketch, "E1.4.10.2", {"start": v(505.36, 460.02) * mm, "end": v(505.36, 453.16) * mm});
            skLineSegment(sketch, "E1.4.10.3", {"start": v(407.57, 460.02) * mm, "end": v(407.57, 453.16) * mm});
            skLineSegment(sketch, "E1.4.11.0", {"start": v(407.57, 499.39) * mm, "end": v(505.36, 499.39) * mm});
            skLineSegment(sketch, "E1.4.11.1", {"start": v(407.57, 492.53) * mm, "end": v(505.36, 492.53) * mm});
            skLineSegment(sketch, "E1.4.11.2", {"start": v(505.36, 499.39) * mm, "end": v(505.36, 492.53) * mm});
            skLineSegment(sketch, "E1.4.11.3", {"start": v(407.57, 499.39) * mm, "end": v(407.57, 492.53) * mm});
            skLineSegment(sketch, "E1.4.12.0", {"start": v(407.57, 538.76) * mm, "end": v(505.36, 538.76) * mm});
            skLineSegment(sketch, "E1.4.12.1", {"start": v(407.57, 531.9) * mm, "end": v(505.36, 531.9) * mm});
            skLineSegment(sketch, "E1.4.12.2", {"start": v(505.36, 538.76) * mm, "end": v(505.36, 531.9) * mm});
            skLineSegment(sketch, "E1.4.12.3", {"start": v(407.57, 538.76) * mm, "end": v(407.57, 531.9) * mm});
            skLineSegment(sketch, "E1.4.13.0", {"start": v(407.57, 578.13) * mm, "end": v(505.36, 578.13) * mm});
            skLineSegment(sketch, "E1.4.13.1", {"start": v(407.57, 571.27) * mm, "end": v(505.36, 571.27) * mm});
            skLineSegment(sketch, "E1.4.13.2", {"start": v(505.36, 578.13) * mm, "end": v(505.36, 571.27) * mm});
            skLineSegment(sketch, "E1.4.13.3", {"start": v(407.57, 578.13) * mm, "end": v(407.57, 571.27) * mm});
            skLineSegment(sketch, "E1.4.14.0", {"start": v(407.57, 617.5) * mm, "end": v(505.36, 617.5) * mm});
            skLineSegment(sketch, "E1.4.14.1", {"start": v(407.57, 610.64) * mm, "end": v(505.36, 610.64) * mm});
            skLineSegment(sketch, "E1.4.14.2", {"start": v(505.36, 617.5) * mm, "end": v(505.36, 610.64) * mm});
            skLineSegment(sketch, "E1.4.14.3", {"start": v(407.57, 617.5) * mm, "end": v(407.57, 610.64) * mm});
            skLineSegment(sketch, "E1.4.15.0", {"start": v(407.57, 656.87) * mm, "end": v(505.36, 656.87) * mm});
            skLineSegment(sketch, "E1.4.15.1", {"start": v(407.57, 650.01) * mm, "end": v(505.36, 650.01) * mm});
            skLineSegment(sketch, "E1.4.15.2", {"start": v(505.36, 656.87) * mm, "end": v(505.36, 650.01) * mm});
            skLineSegment(sketch, "E1.4.15.3", {"start": v(407.57, 656.87) * mm, "end": v(407.57, 650.01) * mm});
            skLineSegment(sketch, "E1.4.16.0", {"start": v(407.57, 696.24) * mm, "end": v(505.36, 696.24) * mm});
            skLineSegment(sketch, "E1.4.16.1", {"start": v(407.57, 689.38) * mm, "end": v(505.36, 689.38) * mm});
            skLineSegment(sketch, "E1.4.16.2", {"start": v(505.36, 696.24) * mm, "end": v(505.36, 689.38) * mm});
            skLineSegment(sketch, "E1.4.16.3", {"start": v(407.57, 696.24) * mm, "end": v(407.57, 689.38) * mm});
            skLineSegment(sketch, "E1.4.17.0", {"start": v(407.57, 735.6) * mm, "end": v(505.36, 735.6) * mm});
            skLineSegment(sketch, "E1.4.17.1", {"start": v(407.57, 728.75) * mm, "end": v(505.36, 728.75) * mm});
            skLineSegment(sketch, "E1.4.17.2", {"start": v(505.36, 735.6) * mm, "end": v(505.36, 728.75) * mm});
            skLineSegment(sketch, "E1.4.17.3", {"start": v(407.57, 735.6) * mm, "end": v(407.57, 728.75) * mm});
            skLineSegment(sketch, "E1.4.18.0", {"start": v(407.57, 774.98) * mm, "end": v(505.36, 774.98) * mm});
            skLineSegment(sketch, "E1.4.18.1", {"start": v(407.57, 768.12) * mm, "end": v(505.36, 768.12) * mm});
            skLineSegment(sketch, "E1.4.18.2", {"start": v(505.36, 774.98) * mm, "end": v(505.36, 768.12) * mm});
            skLineSegment(sketch, "E1.4.18.3", {"start": v(407.57, 774.98) * mm, "end": v(407.57, 768.12) * mm});
            skLineSegment(sketch, "E1.4.19.0", {"start": v(407.57, 814.35) * mm, "end": v(505.36, 814.35) * mm});
            skLineSegment(sketch, "E1.4.19.1", {"start": v(407.57, 807.5) * mm, "end": v(505.36, 807.5) * mm});
            skLineSegment(sketch, "E1.4.19.2", {"start": v(505.36, 814.35) * mm, "end": v(505.36, 807.5) * mm});
            skLineSegment(sketch, "E1.4.19.3", {"start": v(407.57, 814.35) * mm, "end": v(407.57, 807.5) * mm});
            skLineSegment(sketch, "E1.4.20.0", {"start": v(407.57, 853.72) * mm, "end": v(505.36, 853.72) * mm});
            skLineSegment(sketch, "E1.4.20.1", {"start": v(407.57, 846.86) * mm, "end": v(505.36, 846.86) * mm});
            skLineSegment(sketch, "E1.4.20.2", {"start": v(505.36, 853.72) * mm, "end": v(505.36, 846.86) * mm});
            skLineSegment(sketch, "E1.4.20.3", {"start": v(407.57, 853.72) * mm, "end": v(407.57, 846.86) * mm});
            skLineSegment(sketch, "E1.4.21.0", {"start": v(407.57, 893.09) * mm, "end": v(505.36, 893.09) * mm});
            skLineSegment(sketch, "E1.4.21.1", {"start": v(407.57, 886.23) * mm, "end": v(505.36, 886.23) * mm});
            skLineSegment(sketch, "E1.4.21.2", {"start": v(505.36, 893.09) * mm, "end": v(505.36, 886.23) * mm});
            skLineSegment(sketch, "E1.4.21.3", {"start": v(407.57, 893.09) * mm, "end": v(407.57, 886.23) * mm});
            skLineSegment(sketch, "E1.4.22.0", {"start": v(407.57, 932.46) * mm, "end": v(505.36, 932.46) * mm});
            skLineSegment(sketch, "E1.4.22.1", {"start": v(407.57, 925.6) * mm, "end": v(505.36, 925.6) * mm});
            skLineSegment(sketch, "E1.4.22.2", {"start": v(505.36, 932.46) * mm, "end": v(505.36, 925.6) * mm});
            skLineSegment(sketch, "E1.4.22.3", {"start": v(407.57, 932.46) * mm, "end": v(407.57, 925.6) * mm});
            skLineSegment(sketch, "E1.4.23.0", {"start": v(407.57, 971.83) * mm, "end": v(505.36, 971.83) * mm});
            skLineSegment(sketch, "E1.4.23.1", {"start": v(407.57, 964.97) * mm, "end": v(505.36, 964.97) * mm});
            skLineSegment(sketch, "E1.4.23.2", {"start": v(505.36, 971.83) * mm, "end": v(505.36, 964.97) * mm});
            skLineSegment(sketch, "E1.4.23.3", {"start": v(407.57, 971.83) * mm, "end": v(407.57, 964.97) * mm});
            skLineSegment(sketch, "E1.4.24.0", {"start": v(407.57, 1011.2) * mm, "end": v(505.36, 1011.2) * mm});
            skLineSegment(sketch, "E1.4.24.1", {"start": v(407.57, 1004.34) * mm, "end": v(505.36, 1004.34) * mm});
            skLineSegment(sketch, "E1.4.24.2", {"start": v(505.36, 1011.2) * mm, "end": v(505.36, 1004.34) * mm});
            skLineSegment(sketch, "E1.4.24.3", {"start": v(407.57, 1011.2) * mm, "end": v(407.57, 1004.34) * mm});
            skLineSegment(sketch, "E1.4.25.0", {"start": v(407.57, 1050.57) * mm, "end": v(505.36, 1050.57) * mm});
            skLineSegment(sketch, "E1.4.25.1", {"start": v(407.57, 1043.71) * mm, "end": v(505.36, 1043.71) * mm});
            skLineSegment(sketch, "E1.4.25.2", {"start": v(505.36, 1050.57) * mm, "end": v(505.36, 1043.71) * mm});
            skLineSegment(sketch, "E1.4.25.3", {"start": v(407.57, 1050.57) * mm, "end": v(407.57, 1043.71) * mm});
            skLineSegment(sketch, "E1.4.26.0", {"start": v(407.57, 1089.94) * mm, "end": v(505.36, 1089.94) * mm});
            skLineSegment(sketch, "E1.4.26.1", {"start": v(407.57, 1083.08) * mm, "end": v(505.36, 1083.08) * mm});
            skLineSegment(sketch, "E1.4.26.2", {"start": v(505.36, 1089.94) * mm, "end": v(505.36, 1083.08) * mm});
            skLineSegment(sketch, "E1.4.26.3", {"start": v(407.57, 1089.94) * mm, "end": v(407.57, 1083.08) * mm});
            skLineSegment(sketch, "E1.4.27.0", {"start": v(407.57, 1129.3) * mm, "end": v(505.36, 1129.3) * mm});
            skLineSegment(sketch, "E1.4.27.1", {"start": v(407.57, 1122.45) * mm, "end": v(505.36, 1122.45) * mm});
            skLineSegment(sketch, "E1.4.27.2", {"start": v(505.36, 1129.3) * mm, "end": v(505.36, 1122.45) * mm});
            skLineSegment(sketch, "E1.4.27.3", {"start": v(407.57, 1129.3) * mm, "end": v(407.57, 1122.45) * mm});
            skLineSegment(sketch, "E1.4.28.0", {"start": v(407.57, 1168.68) * mm, "end": v(505.36, 1168.68) * mm});
            skLineSegment(sketch, "E1.4.28.1", {"start": v(407.57, 1161.82) * mm, "end": v(505.36, 1161.82) * mm});
            skLineSegment(sketch, "E1.4.28.2", {"start": v(505.36, 1168.68) * mm, "end": v(505.36, 1161.82) * mm});
            skLineSegment(sketch, "E1.4.28.3", {"start": v(407.57, 1168.68) * mm, "end": v(407.57, 1161.82) * mm});
            skLineSegment(sketch, "E1.4.29.0", {"start": v(407.57, 1208.05) * mm, "end": v(505.36, 1208.05) * mm});
            skLineSegment(sketch, "E1.4.29.1", {"start": v(407.57, 1201.2) * mm, "end": v(505.36, 1201.2) * mm});
            skLineSegment(sketch, "E1.4.29.2", {"start": v(505.36, 1208.05) * mm, "end": v(505.36, 1201.2) * mm});
            skLineSegment(sketch, "E1.4.29.3", {"start": v(407.57, 1208.05) * mm, "end": v(407.57, 1201.2) * mm});
            skLineSegment(sketch, "E1.5.0.0", {"start": v(535.6, 66.32) * mm, "end": v(633.38, 66.32) * mm});
            skLineSegment(sketch, "E1.5.0.1", {"start": v(535.6, 59.46) * mm, "end": v(633.38, 59.46) * mm});
            skLineSegment(sketch, "E1.5.0.2", {"start": v(633.38, 66.32) * mm, "end": v(633.38, 59.46) * mm});
            skLineSegment(sketch, "E1.5.0.3", {"start": v(535.6, 66.32) * mm, "end": v(535.6, 59.46) * mm});
            skLineSegment(sketch, "E1.5.1.0", {"start": v(535.6, 105.69) * mm, "end": v(633.38, 105.69) * mm});
            skLineSegment(sketch, "E1.5.1.1", {"start": v(535.6, 98.83) * mm, "end": v(633.38, 98.83) * mm});
            skLineSegment(sketch, "E1.5.1.2", {"start": v(633.38, 105.69) * mm, "end": v(633.38, 98.83) * mm});
            skLineSegment(sketch, "E1.5.1.3", {"start": v(535.6, 105.69) * mm, "end": v(535.6, 98.83) * mm});
            skLineSegment(sketch, "E1.5.2.0", {"start": v(535.6, 145.06) * mm, "end": v(633.38, 145.06) * mm});
            skLineSegment(sketch, "E1.5.2.1", {"start": v(535.6, 138.2) * mm, "end": v(633.38, 138.2) * mm});
            skLineSegment(sketch, "E1.5.2.2", {"start": v(633.38, 145.06) * mm, "end": v(633.38, 138.2) * mm});
            skLineSegment(sketch, "E1.5.2.3", {"start": v(535.6, 145.06) * mm, "end": v(535.6, 138.2) * mm});
            skLineSegment(sketch, "E1.5.3.0", {"start": v(535.6, 184.43) * mm, "end": v(633.38, 184.43) * mm});
            skLineSegment(sketch, "E1.5.3.1", {"start": v(535.6, 177.57) * mm, "end": v(633.38, 177.57) * mm});
            skLineSegment(sketch, "E1.5.3.2", {"start": v(633.38, 184.43) * mm, "end": v(633.38, 177.57) * mm});
            skLineSegment(sketch, "E1.5.3.3", {"start": v(535.6, 184.43) * mm, "end": v(535.6, 177.57) * mm});
            skLineSegment(sketch, "E1.5.4.0", {"start": v(535.6, 223.8) * mm, "end": v(633.38, 223.8) * mm});
            skLineSegment(sketch, "E1.5.4.1", {"start": v(535.6, 216.94) * mm, "end": v(633.38, 216.94) * mm});
            skLineSegment(sketch, "E1.5.4.2", {"start": v(633.38, 223.8) * mm, "end": v(633.38, 216.94) * mm});
            skLineSegment(sketch, "E1.5.4.3", {"start": v(535.6, 223.8) * mm, "end": v(535.6, 216.94) * mm});
            skLineSegment(sketch, "E1.5.5.0", {"start": v(535.6, 263.17) * mm, "end": v(633.38, 263.17) * mm});
            skLineSegment(sketch, "E1.5.5.1", {"start": v(535.6, 256.31) * mm, "end": v(633.38, 256.31) * mm});
            skLineSegment(sketch, "E1.5.5.2", {"start": v(633.38, 263.17) * mm, "end": v(633.38, 256.31) * mm});
            skLineSegment(sketch, "E1.5.5.3", {"start": v(535.6, 263.17) * mm, "end": v(535.6, 256.31) * mm});
            skLineSegment(sketch, "E1.5.6.0", {"start": v(535.6, 302.54) * mm, "end": v(633.38, 302.54) * mm});
            skLineSegment(sketch, "E1.5.6.1", {"start": v(535.6, 295.68) * mm, "end": v(633.38, 295.68) * mm});
            skLineSegment(sketch, "E1.5.6.2", {"start": v(633.38, 302.54) * mm, "end": v(633.38, 295.68) * mm});
            skLineSegment(sketch, "E1.5.6.3", {"start": v(535.6, 302.54) * mm, "end": v(535.6, 295.68) * mm});
            skLineSegment(sketch, "E1.5.7.0", {"start": v(535.6, 341.9) * mm, "end": v(633.38, 341.9) * mm});
            skLineSegment(sketch, "E1.5.7.1", {"start": v(535.6, 335.05) * mm, "end": v(633.38, 335.05) * mm});
            skLineSegment(sketch, "E1.5.7.2", {"start": v(633.38, 341.9) * mm, "end": v(633.38, 335.05) * mm});
            skLineSegment(sketch, "E1.5.7.3", {"start": v(535.6, 341.9) * mm, "end": v(535.6, 335.05) * mm});
            skLineSegment(sketch, "E1.5.8.0", {"start": v(535.6, 381.28) * mm, "end": v(633.38, 381.28) * mm});
            skLineSegment(sketch, "E1.5.8.1", {"start": v(535.6, 374.42) * mm, "end": v(633.38, 374.42) * mm});
            skLineSegment(sketch, "E1.5.8.2", {"start": v(633.38, 381.28) * mm, "end": v(633.38, 374.42) * mm});
            skLineSegment(sketch, "E1.5.8.3", {"start": v(535.6, 381.28) * mm, "end": v(535.6, 374.42) * mm});
            skLineSegment(sketch, "E1.5.9.0", {"start": v(535.6, 420.65) * mm, "end": v(633.38, 420.65) * mm});
            skLineSegment(sketch, "E1.5.9.1", {"start": v(535.6, 413.8) * mm, "end": v(633.38, 413.8) * mm});
            skLineSegment(sketch, "E1.5.9.2", {"start": v(633.38, 420.65) * mm, "end": v(633.38, 413.8) * mm});
            skLineSegment(sketch, "E1.5.9.3", {"start": v(535.6, 420.65) * mm, "end": v(535.6, 413.8) * mm});
            skLineSegment(sketch, "E1.5.10.0", {"start": v(535.6, 460.02) * mm, "end": v(633.38, 460.02) * mm});
            skLineSegment(sketch, "E1.5.10.1", {"start": v(535.6, 453.16) * mm, "end": v(633.38, 453.16) * mm});
            skLineSegment(sketch, "E1.5.10.2", {"start": v(633.38, 460.02) * mm, "end": v(633.38, 453.16) * mm});
            skLineSegment(sketch, "E1.5.10.3", {"start": v(535.6, 460.02) * mm, "end": v(535.6, 453.16) * mm});
            skLineSegment(sketch, "E1.5.11.0", {"start": v(535.6, 499.39) * mm, "end": v(633.38, 499.39) * mm});
            skLineSegment(sketch, "E1.5.11.1", {"start": v(535.6, 492.53) * mm, "end": v(633.38, 492.53) * mm});
            skLineSegment(sketch, "E1.5.11.2", {"start": v(633.38, 499.39) * mm, "end": v(633.38, 492.53) * mm});
            skLineSegment(sketch, "E1.5.11.3", {"start": v(535.6, 499.39) * mm, "end": v(535.6, 492.53) * mm});
            skLineSegment(sketch, "E1.5.12.0", {"start": v(535.6, 538.76) * mm, "end": v(633.38, 538.76) * mm});
            skLineSegment(sketch, "E1.5.12.1", {"start": v(535.6, 531.9) * mm, "end": v(633.38, 531.9) * mm});
            skLineSegment(sketch, "E1.5.12.2", {"start": v(633.38, 538.76) * mm, "end": v(633.38, 531.9) * mm});
            skLineSegment(sketch, "E1.5.12.3", {"start": v(535.6, 538.76) * mm, "end": v(535.6, 531.9) * mm});
            skLineSegment(sketch, "E1.5.13.0", {"start": v(535.6, 578.13) * mm, "end": v(633.38, 578.13) * mm});
            skLineSegment(sketch, "E1.5.13.1", {"start": v(535.6, 571.27) * mm, "end": v(633.38, 571.27) * mm});
            skLineSegment(sketch, "E1.5.13.2", {"start": v(633.38, 578.13) * mm, "end": v(633.38, 571.27) * mm});
            skLineSegment(sketch, "E1.5.13.3", {"start": v(535.6, 578.13) * mm, "end": v(535.6, 571.27) * mm});
            skLineSegment(sketch, "E1.5.14.0", {"start": v(535.6, 617.5) * mm, "end": v(633.38, 617.5) * mm});
            skLineSegment(sketch, "E1.5.14.1", {"start": v(535.6, 610.64) * mm, "end": v(633.38, 610.64) * mm});
            skLineSegment(sketch, "E1.5.14.2", {"start": v(633.38, 617.5) * mm, "end": v(633.38, 610.64) * mm});
            skLineSegment(sketch, "E1.5.14.3", {"start": v(535.6, 617.5) * mm, "end": v(535.6, 610.64) * mm});
            skLineSegment(sketch, "E1.5.15.0", {"start": v(535.6, 656.87) * mm, "end": v(633.38, 656.87) * mm});
            skLineSegment(sketch, "E1.5.15.1", {"start": v(535.6, 650.01) * mm, "end": v(633.38, 650.01) * mm});
            skLineSegment(sketch, "E1.5.15.2", {"start": v(633.38, 656.87) * mm, "end": v(633.38, 650.01) * mm});
            skLineSegment(sketch, "E1.5.15.3", {"start": v(535.6, 656.87) * mm, "end": v(535.6, 650.01) * mm});
            skLineSegment(sketch, "E1.5.16.0", {"start": v(535.6, 696.24) * mm, "end": v(633.38, 696.24) * mm});
            skLineSegment(sketch, "E1.5.16.1", {"start": v(535.6, 689.38) * mm, "end": v(633.38, 689.38) * mm});
            skLineSegment(sketch, "E1.5.16.2", {"start": v(633.38, 696.24) * mm, "end": v(633.38, 689.38) * mm});
            skLineSegment(sketch, "E1.5.16.3", {"start": v(535.6, 696.24) * mm, "end": v(535.6, 689.38) * mm});
            skLineSegment(sketch, "E1.5.17.0", {"start": v(535.6, 735.6) * mm, "end": v(633.38, 735.6) * mm});
            skLineSegment(sketch, "E1.5.17.1", {"start": v(535.6, 728.75) * mm, "end": v(633.38, 728.75) * mm});
            skLineSegment(sketch, "E1.5.17.2", {"start": v(633.38, 735.6) * mm, "end": v(633.38, 728.75) * mm});
            skLineSegment(sketch, "E1.5.17.3", {"start": v(535.6, 735.6) * mm, "end": v(535.6, 728.75) * mm});
            skLineSegment(sketch, "E1.5.18.0", {"start": v(535.6, 774.98) * mm, "end": v(633.38, 774.98) * mm});
            skLineSegment(sketch, "E1.5.18.1", {"start": v(535.6, 768.12) * mm, "end": v(633.38, 768.12) * mm});
            skLineSegment(sketch, "E1.5.18.2", {"start": v(633.38, 774.98) * mm, "end": v(633.38, 768.12) * mm});
            skLineSegment(sketch, "E1.5.18.3", {"start": v(535.6, 774.98) * mm, "end": v(535.6, 768.12) * mm});
            skLineSegment(sketch, "E1.5.19.0", {"start": v(535.6, 814.35) * mm, "end": v(633.38, 814.35) * mm});
            skLineSegment(sketch, "E1.5.19.1", {"start": v(535.6, 807.5) * mm, "end": v(633.38, 807.5) * mm});
            skLineSegment(sketch, "E1.5.19.2", {"start": v(633.38, 814.35) * mm, "end": v(633.38, 807.5) * mm});
            skLineSegment(sketch, "E1.5.19.3", {"start": v(535.6, 814.35) * mm, "end": v(535.6, 807.5) * mm});
            skLineSegment(sketch, "E1.5.20.0", {"start": v(535.6, 853.72) * mm, "end": v(633.38, 853.72) * mm});
            skLineSegment(sketch, "E1.5.20.1", {"start": v(535.6, 846.86) * mm, "end": v(633.38, 846.86) * mm});
            skLineSegment(sketch, "E1.5.20.2", {"start": v(633.38, 853.72) * mm, "end": v(633.38, 846.86) * mm});
            skLineSegment(sketch, "E1.5.20.3", {"start": v(535.6, 853.72) * mm, "end": v(535.6, 846.86) * mm});
            skLineSegment(sketch, "E1.5.21.0", {"start": v(535.6, 893.09) * mm, "end": v(633.38, 893.09) * mm});
            skLineSegment(sketch, "E1.5.21.1", {"start": v(535.6, 886.23) * mm, "end": v(633.38, 886.23) * mm});
            skLineSegment(sketch, "E1.5.21.2", {"start": v(633.38, 893.09) * mm, "end": v(633.38, 886.23) * mm});
            skLineSegment(sketch, "E1.5.21.3", {"start": v(535.6, 893.09) * mm, "end": v(535.6, 886.23) * mm});
            skLineSegment(sketch, "E1.5.22.0", {"start": v(535.6, 932.46) * mm, "end": v(633.38, 932.46) * mm});
            skLineSegment(sketch, "E1.5.22.1", {"start": v(535.6, 925.6) * mm, "end": v(633.38, 925.6) * mm});
            skLineSegment(sketch, "E1.5.22.2", {"start": v(633.38, 932.46) * mm, "end": v(633.38, 925.6) * mm});
            skLineSegment(sketch, "E1.5.22.3", {"start": v(535.6, 932.46) * mm, "end": v(535.6, 925.6) * mm});
            skLineSegment(sketch, "E1.5.23.0", {"start": v(535.6, 971.83) * mm, "end": v(633.38, 971.83) * mm});
            skLineSegment(sketch, "E1.5.23.1", {"start": v(535.6, 964.97) * mm, "end": v(633.38, 964.97) * mm});
            skLineSegment(sketch, "E1.5.23.2", {"start": v(633.38, 971.83) * mm, "end": v(633.38, 964.97) * mm});
            skLineSegment(sketch, "E1.5.23.3", {"start": v(535.6, 971.83) * mm, "end": v(535.6, 964.97) * mm});
            skLineSegment(sketch, "E1.5.24.0", {"start": v(535.6, 1011.2) * mm, "end": v(633.38, 1011.2) * mm});
            skLineSegment(sketch, "E1.5.24.1", {"start": v(535.6, 1004.34) * mm, "end": v(633.38, 1004.34) * mm});
            skLineSegment(sketch, "E1.5.24.2", {"start": v(633.38, 1011.2) * mm, "end": v(633.38, 1004.34) * mm});
            skLineSegment(sketch, "E1.5.24.3", {"start": v(535.6, 1011.2) * mm, "end": v(535.6, 1004.34) * mm});
            skLineSegment(sketch, "E1.5.25.0", {"start": v(535.6, 1050.57) * mm, "end": v(633.38, 1050.57) * mm});
            skLineSegment(sketch, "E1.5.25.1", {"start": v(535.6, 1043.71) * mm, "end": v(633.38, 1043.71) * mm});
            skLineSegment(sketch, "E1.5.25.2", {"start": v(633.38, 1050.57) * mm, "end": v(633.38, 1043.71) * mm});
            skLineSegment(sketch, "E1.5.25.3", {"start": v(535.6, 1050.57) * mm, "end": v(535.6, 1043.71) * mm});
            skLineSegment(sketch, "E1.5.26.0", {"start": v(535.6, 1089.94) * mm, "end": v(633.38, 1089.94) * mm});
            skLineSegment(sketch, "E1.5.26.1", {"start": v(535.6, 1083.08) * mm, "end": v(633.38, 1083.08) * mm});
            skLineSegment(sketch, "E1.5.26.2", {"start": v(633.38, 1089.94) * mm, "end": v(633.38, 1083.08) * mm});
            skLineSegment(sketch, "E1.5.26.3", {"start": v(535.6, 1089.94) * mm, "end": v(535.6, 1083.08) * mm});
            skLineSegment(sketch, "E1.5.27.0", {"start": v(535.6, 1129.3) * mm, "end": v(633.38, 1129.3) * mm});
            skLineSegment(sketch, "E1.5.27.1", {"start": v(535.6, 1122.45) * mm, "end": v(633.38, 1122.45) * mm});
            skLineSegment(sketch, "E1.5.27.2", {"start": v(633.38, 1129.3) * mm, "end": v(633.38, 1122.45) * mm});
            skLineSegment(sketch, "E1.5.27.3", {"start": v(535.6, 1129.3) * mm, "end": v(535.6, 1122.45) * mm});
            skLineSegment(sketch, "E1.5.28.0", {"start": v(535.6, 1168.68) * mm, "end": v(633.38, 1168.68) * mm});
            skLineSegment(sketch, "E1.5.28.1", {"start": v(535.6, 1161.82) * mm, "end": v(633.38, 1161.82) * mm});
            skLineSegment(sketch, "E1.5.28.2", {"start": v(633.38, 1168.68) * mm, "end": v(633.38, 1161.82) * mm});
            skLineSegment(sketch, "E1.5.28.3", {"start": v(535.6, 1168.68) * mm, "end": v(535.6, 1161.82) * mm});
            skLineSegment(sketch, "E1.5.29.0", {"start": v(535.6, 1208.05) * mm, "end": v(633.38, 1208.05) * mm});
            skLineSegment(sketch, "E1.5.29.1", {"start": v(535.6, 1201.2) * mm, "end": v(633.38, 1201.2) * mm});
            skLineSegment(sketch, "E1.5.29.2", {"start": v(633.38, 1208.05) * mm, "end": v(633.38, 1201.2) * mm});
            skLineSegment(sketch, "E1.5.29.3", {"start": v(535.6, 1208.05) * mm, "end": v(535.6, 1201.2) * mm});
            skLineSegment(sketch, "E1.6.0.0", {"start": v(663.6, 66.32) * mm, "end": v(761.4, 66.32) * mm});
            skLineSegment(sketch, "E1.6.0.1", {"start": v(663.6, 59.46) * mm, "end": v(761.4, 59.46) * mm});
            skLineSegment(sketch, "E1.6.0.2", {"start": v(761.4, 66.32) * mm, "end": v(761.4, 59.46) * mm});
            skLineSegment(sketch, "E1.6.0.3", {"start": v(663.6, 66.32) * mm, "end": v(663.6, 59.46) * mm});
            skLineSegment(sketch, "E1.6.1.0", {"start": v(663.6, 105.69) * mm, "end": v(761.4, 105.69) * mm});
            skLineSegment(sketch, "E1.6.1.1", {"start": v(663.6, 98.83) * mm, "end": v(761.4, 98.83) * mm});
            skLineSegment(sketch, "E1.6.1.2", {"start": v(761.4, 105.69) * mm, "end": v(761.4, 98.83) * mm});
            skLineSegment(sketch, "E1.6.1.3", {"start": v(663.6, 105.69) * mm, "end": v(663.6, 98.83) * mm});
            skLineSegment(sketch, "E1.6.2.0", {"start": v(663.6, 145.06) * mm, "end": v(761.4, 145.06) * mm});
            skLineSegment(sketch, "E1.6.2.1", {"start": v(663.6, 138.2) * mm, "end": v(761.4, 138.2) * mm});
            skLineSegment(sketch, "E1.6.2.2", {"start": v(761.4, 145.06) * mm, "end": v(761.4, 138.2) * mm});
            skLineSegment(sketch, "E1.6.2.3", {"start": v(663.6, 145.06) * mm, "end": v(663.6, 138.2) * mm});
            skLineSegment(sketch, "E1.6.3.0", {"start": v(663.6, 184.43) * mm, "end": v(761.4, 184.43) * mm});
            skLineSegment(sketch, "E1.6.3.1", {"start": v(663.6, 177.57) * mm, "end": v(761.4, 177.57) * mm});
            skLineSegment(sketch, "E1.6.3.2", {"start": v(761.4, 184.43) * mm, "end": v(761.4, 177.57) * mm});
            skLineSegment(sketch, "E1.6.3.3", {"start": v(663.6, 184.43) * mm, "end": v(663.6, 177.57) * mm});
            skLineSegment(sketch, "E1.6.4.0", {"start": v(663.6, 223.8) * mm, "end": v(761.4, 223.8) * mm});
            skLineSegment(sketch, "E1.6.4.1", {"start": v(663.6, 216.94) * mm, "end": v(761.4, 216.94) * mm});
            skLineSegment(sketch, "E1.6.4.2", {"start": v(761.4, 223.8) * mm, "end": v(761.4, 216.94) * mm});
            skLineSegment(sketch, "E1.6.4.3", {"start": v(663.6, 223.8) * mm, "end": v(663.6, 216.94) * mm});
            skLineSegment(sketch, "E1.6.5.0", {"start": v(663.6, 263.17) * mm, "end": v(761.4, 263.17) * mm});
            skLineSegment(sketch, "E1.6.5.1", {"start": v(663.6, 256.31) * mm, "end": v(761.4, 256.31) * mm});
            skLineSegment(sketch, "E1.6.5.2", {"start": v(761.4, 263.17) * mm, "end": v(761.4, 256.31) * mm});
            skLineSegment(sketch, "E1.6.5.3", {"start": v(663.6, 263.17) * mm, "end": v(663.6, 256.31) * mm});
            skLineSegment(sketch, "E1.6.6.0", {"start": v(663.6, 302.54) * mm, "end": v(761.4, 302.54) * mm});
            skLineSegment(sketch, "E1.6.6.1", {"start": v(663.6, 295.68) * mm, "end": v(761.4, 295.68) * mm});
            skLineSegment(sketch, "E1.6.6.2", {"start": v(761.4, 302.54) * mm, "end": v(761.4, 295.68) * mm});
            skLineSegment(sketch, "E1.6.6.3", {"start": v(663.6, 302.54) * mm, "end": v(663.6, 295.68) * mm});
            skLineSegment(sketch, "E1.6.7.0", {"start": v(663.6, 341.9) * mm, "end": v(761.4, 341.9) * mm});
            skLineSegment(sketch, "E1.6.7.1", {"start": v(663.6, 335.05) * mm, "end": v(761.4, 335.05) * mm});
            skLineSegment(sketch, "E1.6.7.2", {"start": v(761.4, 341.9) * mm, "end": v(761.4, 335.05) * mm});
            skLineSegment(sketch, "E1.6.7.3", {"start": v(663.6, 341.9) * mm, "end": v(663.6, 335.05) * mm});
            skLineSegment(sketch, "E1.6.8.0", {"start": v(663.6, 381.28) * mm, "end": v(761.4, 381.28) * mm});
            skLineSegment(sketch, "E1.6.8.1", {"start": v(663.6, 374.42) * mm, "end": v(761.4, 374.42) * mm});
            skLineSegment(sketch, "E1.6.8.2", {"start": v(761.4, 381.28) * mm, "end": v(761.4, 374.42) * mm});
            skLineSegment(sketch, "E1.6.8.3", {"start": v(663.6, 381.28) * mm, "end": v(663.6, 374.42) * mm});
            skLineSegment(sketch, "E1.6.9.0", {"start": v(663.6, 420.65) * mm, "end": v(761.4, 420.65) * mm});
            skLineSegment(sketch, "E1.6.9.1", {"start": v(663.6, 413.8) * mm, "end": v(761.4, 413.8) * mm});
            skLineSegment(sketch, "E1.6.9.2", {"start": v(761.4, 420.65) * mm, "end": v(761.4, 413.8) * mm});
            skLineSegment(sketch, "E1.6.9.3", {"start": v(663.6, 420.65) * mm, "end": v(663.6, 413.8) * mm});
            skLineSegment(sketch, "E1.6.10.0", {"start": v(663.6, 460.02) * mm, "end": v(761.4, 460.02) * mm});
            skLineSegment(sketch, "E1.6.10.1", {"start": v(663.6, 453.16) * mm, "end": v(761.4, 453.16) * mm});
            skLineSegment(sketch, "E1.6.10.2", {"start": v(761.4, 460.02) * mm, "end": v(761.4, 453.16) * mm});
            skLineSegment(sketch, "E1.6.10.3", {"start": v(663.6, 460.02) * mm, "end": v(663.6, 453.16) * mm});
            skLineSegment(sketch, "E1.6.11.0", {"start": v(663.6, 499.39) * mm, "end": v(761.4, 499.39) * mm});
            skLineSegment(sketch, "E1.6.11.1", {"start": v(663.6, 492.53) * mm, "end": v(761.4, 492.53) * mm});
            skLineSegment(sketch, "E1.6.11.2", {"start": v(761.4, 499.39) * mm, "end": v(761.4, 492.53) * mm});
            skLineSegment(sketch, "E1.6.11.3", {"start": v(663.6, 499.39) * mm, "end": v(663.6, 492.53) * mm});
            skLineSegment(sketch, "E1.6.12.0", {"start": v(663.6, 538.76) * mm, "end": v(761.4, 538.76) * mm});
            skLineSegment(sketch, "E1.6.12.1", {"start": v(663.6, 531.9) * mm, "end": v(761.4, 531.9) * mm});
            skLineSegment(sketch, "E1.6.12.2", {"start": v(761.4, 538.76) * mm, "end": v(761.4, 531.9) * mm});
            skLineSegment(sketch, "E1.6.12.3", {"start": v(663.6, 538.76) * mm, "end": v(663.6, 531.9) * mm});
            skLineSegment(sketch, "E1.6.13.0", {"start": v(663.6, 578.13) * mm, "end": v(761.4, 578.13) * mm});
            skLineSegment(sketch, "E1.6.13.1", {"start": v(663.6, 571.27) * mm, "end": v(761.4, 571.27) * mm});
            skLineSegment(sketch, "E1.6.13.2", {"start": v(761.4, 578.13) * mm, "end": v(761.4, 571.27) * mm});
            skLineSegment(sketch, "E1.6.13.3", {"start": v(663.6, 578.13) * mm, "end": v(663.6, 571.27) * mm});
            skLineSegment(sketch, "E1.6.14.0", {"start": v(663.6, 617.5) * mm, "end": v(761.4, 617.5) * mm});
            skLineSegment(sketch, "E1.6.14.1", {"start": v(663.6, 610.64) * mm, "end": v(761.4, 610.64) * mm});
            skLineSegment(sketch, "E1.6.14.2", {"start": v(761.4, 617.5) * mm, "end": v(761.4, 610.64) * mm});
            skLineSegment(sketch, "E1.6.14.3", {"start": v(663.6, 617.5) * mm, "end": v(663.6, 610.64) * mm});
            skLineSegment(sketch, "E1.6.15.0", {"start": v(663.6, 656.87) * mm, "end": v(761.4, 656.87) * mm});
            skLineSegment(sketch, "E1.6.15.1", {"start": v(663.6, 650.01) * mm, "end": v(761.4, 650.01) * mm});
            skLineSegment(sketch, "E1.6.15.2", {"start": v(761.4, 656.87) * mm, "end": v(761.4, 650.01) * mm});
            skLineSegment(sketch, "E1.6.15.3", {"start": v(663.6, 656.87) * mm, "end": v(663.6, 650.01) * mm});
            skLineSegment(sketch, "E1.6.16.0", {"start": v(663.6, 696.24) * mm, "end": v(761.4, 696.24) * mm});
            skLineSegment(sketch, "E1.6.16.1", {"start": v(663.6, 689.38) * mm, "end": v(761.4, 689.38) * mm});
            skLineSegment(sketch, "E1.6.16.2", {"start": v(761.4, 696.24) * mm, "end": v(761.4, 689.38) * mm});
            skLineSegment(sketch, "E1.6.16.3", {"start": v(663.6, 696.24) * mm, "end": v(663.6, 689.38) * mm});
            skLineSegment(sketch, "E1.6.17.0", {"start": v(663.6, 735.6) * mm, "end": v(761.4, 735.6) * mm});
            skLineSegment(sketch, "E1.6.17.1", {"start": v(663.6, 728.75) * mm, "end": v(761.4, 728.75) * mm});
            skLineSegment(sketch, "E1.6.17.2", {"start": v(761.4, 735.6) * mm, "end": v(761.4, 728.75) * mm});
            skLineSegment(sketch, "E1.6.17.3", {"start": v(663.6, 735.6) * mm, "end": v(663.6, 728.75) * mm});
            skLineSegment(sketch, "E1.6.18.0", {"start": v(663.6, 774.98) * mm, "end": v(761.4, 774.98) * mm});
            skLineSegment(sketch, "E1.6.18.1", {"start": v(663.6, 768.12) * mm, "end": v(761.4, 768.12) * mm});
            skLineSegment(sketch, "E1.6.18.2", {"start": v(761.4, 774.98) * mm, "end": v(761.4, 768.12) * mm});
            skLineSegment(sketch, "E1.6.18.3", {"start": v(663.6, 774.98) * mm, "end": v(663.6, 768.12) * mm});
            skLineSegment(sketch, "E1.6.19.0", {"start": v(663.6, 814.35) * mm, "end": v(761.4, 814.35) * mm});
            skLineSegment(sketch, "E1.6.19.1", {"start": v(663.6, 807.5) * mm, "end": v(761.4, 807.5) * mm});
            skLineSegment(sketch, "E1.6.19.2", {"start": v(761.4, 814.35) * mm, "end": v(761.4, 807.5) * mm});
            skLineSegment(sketch, "E1.6.19.3", {"start": v(663.6, 814.35) * mm, "end": v(663.6, 807.5) * mm});
            skLineSegment(sketch, "E1.6.20.0", {"start": v(663.6, 853.72) * mm, "end": v(761.4, 853.72) * mm});
            skLineSegment(sketch, "E1.6.20.1", {"start": v(663.6, 846.86) * mm, "end": v(761.4, 846.86) * mm});
            skLineSegment(sketch, "E1.6.20.2", {"start": v(761.4, 853.72) * mm, "end": v(761.4, 846.86) * mm});
            skLineSegment(sketch, "E1.6.20.3", {"start": v(663.6, 853.72) * mm, "end": v(663.6, 846.86) * mm});
            skLineSegment(sketch, "E1.6.21.0", {"start": v(663.6, 893.09) * mm, "end": v(761.4, 893.09) * mm});
            skLineSegment(sketch, "E1.6.21.1", {"start": v(663.6, 886.23) * mm, "end": v(761.4, 886.23) * mm});
            skLineSegment(sketch, "E1.6.21.2", {"start": v(761.4, 893.09) * mm, "end": v(761.4, 886.23) * mm});
            skLineSegment(sketch, "E1.6.21.3", {"start": v(663.6, 893.09) * mm, "end": v(663.6, 886.23) * mm});
            skLineSegment(sketch, "E1.6.22.0", {"start": v(663.6, 932.46) * mm, "end": v(761.4, 932.46) * mm});
            skLineSegment(sketch, "E1.6.22.1", {"start": v(663.6, 925.6) * mm, "end": v(761.4, 925.6) * mm});
            skLineSegment(sketch, "E1.6.22.2", {"start": v(761.4, 932.46) * mm, "end": v(761.4, 925.6) * mm});
            skLineSegment(sketch, "E1.6.22.3", {"start": v(663.6, 932.46) * mm, "end": v(663.6, 925.6) * mm});
            skLineSegment(sketch, "E1.6.23.0", {"start": v(663.6, 971.83) * mm, "end": v(761.4, 971.83) * mm});
            skLineSegment(sketch, "E1.6.23.1", {"start": v(663.6, 964.97) * mm, "end": v(761.4, 964.97) * mm});
            skLineSegment(sketch, "E1.6.23.2", {"start": v(761.4, 971.83) * mm, "end": v(761.4, 964.97) * mm});
            skLineSegment(sketch, "E1.6.23.3", {"start": v(663.6, 971.83) * mm, "end": v(663.6, 964.97) * mm});
            skLineSegment(sketch, "E1.6.24.0", {"start": v(663.6, 1011.2) * mm, "end": v(761.4, 1011.2) * mm});
            skLineSegment(sketch, "E1.6.24.1", {"start": v(663.6, 1004.34) * mm, "end": v(761.4, 1004.34) * mm});
            skLineSegment(sketch, "E1.6.24.2", {"start": v(761.4, 1011.2) * mm, "end": v(761.4, 1004.34) * mm});
            skLineSegment(sketch, "E1.6.24.3", {"start": v(663.6, 1011.2) * mm, "end": v(663.6, 1004.34) * mm});
            skLineSegment(sketch, "E1.6.25.0", {"start": v(663.6, 1050.57) * mm, "end": v(761.4, 1050.57) * mm});
            skLineSegment(sketch, "E1.6.25.1", {"start": v(663.6, 1043.71) * mm, "end": v(761.4, 1043.71) * mm});
            skLineSegment(sketch, "E1.6.25.2", {"start": v(761.4, 1050.57) * mm, "end": v(761.4, 1043.71) * mm});
            skLineSegment(sketch, "E1.6.25.3", {"start": v(663.6, 1050.57) * mm, "end": v(663.6, 1043.71) * mm});
            skLineSegment(sketch, "E1.6.26.0", {"start": v(663.6, 1089.94) * mm, "end": v(761.4, 1089.94) * mm});
            skLineSegment(sketch, "E1.6.26.1", {"start": v(663.6, 1083.08) * mm, "end": v(761.4, 1083.08) * mm});
            skLineSegment(sketch, "E1.6.26.2", {"start": v(761.4, 1089.94) * mm, "end": v(761.4, 1083.08) * mm});
            skLineSegment(sketch, "E1.6.26.3", {"start": v(663.6, 1089.94) * mm, "end": v(663.6, 1083.08) * mm});
            skLineSegment(sketch, "E1.6.27.0", {"start": v(663.6, 1129.3) * mm, "end": v(761.4, 1129.3) * mm});
            skLineSegment(sketch, "E1.6.27.1", {"start": v(663.6, 1122.45) * mm, "end": v(761.4, 1122.45) * mm});
            skLineSegment(sketch, "E1.6.27.2", {"start": v(761.4, 1129.3) * mm, "end": v(761.4, 1122.45) * mm});
            skLineSegment(sketch, "E1.6.27.3", {"start": v(663.6, 1129.3) * mm, "end": v(663.6, 1122.45) * mm});
            skLineSegment(sketch, "E1.6.28.0", {"start": v(663.6, 1168.68) * mm, "end": v(761.4, 1168.68) * mm});
            skLineSegment(sketch, "E1.6.28.1", {"start": v(663.6, 1161.82) * mm, "end": v(761.4, 1161.82) * mm});
            skLineSegment(sketch, "E1.6.28.2", {"start": v(761.4, 1168.68) * mm, "end": v(761.4, 1161.82) * mm});
            skLineSegment(sketch, "E1.6.28.3", {"start": v(663.6, 1168.68) * mm, "end": v(663.6, 1161.82) * mm});
            skLineSegment(sketch, "E1.6.29.0", {"start": v(663.6, 1208.05) * mm, "end": v(761.4, 1208.05) * mm});
            skLineSegment(sketch, "E1.6.29.1", {"start": v(663.6, 1201.2) * mm, "end": v(761.4, 1201.2) * mm});
            skLineSegment(sketch, "E1.6.29.2", {"start": v(761.4, 1208.05) * mm, "end": v(761.4, 1201.2) * mm});
            skLineSegment(sketch, "E1.6.29.3", {"start": v(663.6, 1208.05) * mm, "end": v(663.6, 1201.2) * mm});
            skLineSegment(sketch, "E1.7.0.0", {"start": v(791.62, 66.32) * mm, "end": v(889.41, 66.32) * mm});
            skLineSegment(sketch, "E1.7.0.1", {"start": v(791.62, 59.46) * mm, "end": v(889.41, 59.46) * mm});
            skLineSegment(sketch, "E1.7.0.2", {"start": v(889.41, 66.32) * mm, "end": v(889.41, 59.46) * mm});
            skLineSegment(sketch, "E1.7.0.3", {"start": v(791.62, 66.32) * mm, "end": v(791.62, 59.46) * mm});
            skLineSegment(sketch, "E1.7.1.0", {"start": v(791.62, 105.69) * mm, "end": v(889.41, 105.69) * mm});
            skLineSegment(sketch, "E1.7.1.1", {"start": v(791.62, 98.83) * mm, "end": v(889.41, 98.83) * mm});
            skLineSegment(sketch, "E1.7.1.2", {"start": v(889.41, 105.69) * mm, "end": v(889.41, 98.83) * mm});
            skLineSegment(sketch, "E1.7.1.3", {"start": v(791.62, 105.69) * mm, "end": v(791.62, 98.83) * mm});
            skLineSegment(sketch, "E1.7.2.0", {"start": v(791.62, 145.06) * mm, "end": v(889.41, 145.06) * mm});
            skLineSegment(sketch, "E1.7.2.1", {"start": v(791.62, 138.2) * mm, "end": v(889.41, 138.2) * mm});
            skLineSegment(sketch, "E1.7.2.2", {"start": v(889.41, 145.06) * mm, "end": v(889.41, 138.2) * mm});
            skLineSegment(sketch, "E1.7.2.3", {"start": v(791.62, 145.06) * mm, "end": v(791.62, 138.2) * mm});
            skLineSegment(sketch, "E1.7.3.0", {"start": v(791.62, 184.43) * mm, "end": v(889.41, 184.43) * mm});
            skLineSegment(sketch, "E1.7.3.1", {"start": v(791.62, 177.57) * mm, "end": v(889.41, 177.57) * mm});
            skLineSegment(sketch, "E1.7.3.2", {"start": v(889.41, 184.43) * mm, "end": v(889.41, 177.57) * mm});
            skLineSegment(sketch, "E1.7.3.3", {"start": v(791.62, 184.43) * mm, "end": v(791.62, 177.57) * mm});
            skLineSegment(sketch, "E1.7.4.0", {"start": v(791.62, 223.8) * mm, "end": v(889.41, 223.8) * mm});
            skLineSegment(sketch, "E1.7.4.1", {"start": v(791.62, 216.94) * mm, "end": v(889.41, 216.94) * mm});
            skLineSegment(sketch, "E1.7.4.2", {"start": v(889.41, 223.8) * mm, "end": v(889.41, 216.94) * mm});
            skLineSegment(sketch, "E1.7.4.3", {"start": v(791.62, 223.8) * mm, "end": v(791.62, 216.94) * mm});
            skLineSegment(sketch, "E1.7.5.0", {"start": v(791.62, 263.17) * mm, "end": v(889.41, 263.17) * mm});
            skLineSegment(sketch, "E1.7.5.1", {"start": v(791.62, 256.31) * mm, "end": v(889.41, 256.31) * mm});
            skLineSegment(sketch, "E1.7.5.2", {"start": v(889.41, 263.17) * mm, "end": v(889.41, 256.31) * mm});
            skLineSegment(sketch, "E1.7.5.3", {"start": v(791.62, 263.17) * mm, "end": v(791.62, 256.31) * mm});
            skLineSegment(sketch, "E1.7.6.0", {"start": v(791.62, 302.54) * mm, "end": v(889.41, 302.54) * mm});
            skLineSegment(sketch, "E1.7.6.1", {"start": v(791.62, 295.68) * mm, "end": v(889.41, 295.68) * mm});
            skLineSegment(sketch, "E1.7.6.2", {"start": v(889.41, 302.54) * mm, "end": v(889.41, 295.68) * mm});
            skLineSegment(sketch, "E1.7.6.3", {"start": v(791.62, 302.54) * mm, "end": v(791.62, 295.68) * mm});
            skLineSegment(sketch, "E1.7.7.0", {"start": v(791.62, 341.9) * mm, "end": v(889.41, 341.9) * mm});
            skLineSegment(sketch, "E1.7.7.1", {"start": v(791.62, 335.05) * mm, "end": v(889.41, 335.05) * mm});
            skLineSegment(sketch, "E1.7.7.2", {"start": v(889.41, 341.9) * mm, "end": v(889.41, 335.05) * mm});
            skLineSegment(sketch, "E1.7.7.3", {"start": v(791.62, 341.9) * mm, "end": v(791.62, 335.05) * mm});
            skLineSegment(sketch, "E1.7.8.0", {"start": v(791.62, 381.28) * mm, "end": v(889.41, 381.28) * mm});
            skLineSegment(sketch, "E1.7.8.1", {"start": v(791.62, 374.42) * mm, "end": v(889.41, 374.42) * mm});
            skLineSegment(sketch, "E1.7.8.2", {"start": v(889.41, 381.28) * mm, "end": v(889.41, 374.42) * mm});
            skLineSegment(sketch, "E1.7.8.3", {"start": v(791.62, 381.28) * mm, "end": v(791.62, 374.42) * mm});
            skLineSegment(sketch, "E1.7.9.0", {"start": v(791.62, 420.65) * mm, "end": v(889.41, 420.65) * mm});
            skLineSegment(sketch, "E1.7.9.1", {"start": v(791.62, 413.8) * mm, "end": v(889.41, 413.8) * mm});
            skLineSegment(sketch, "E1.7.9.2", {"start": v(889.41, 420.65) * mm, "end": v(889.41, 413.8) * mm});
            skLineSegment(sketch, "E1.7.9.3", {"start": v(791.62, 420.65) * mm, "end": v(791.62, 413.8) * mm});
            skLineSegment(sketch, "E1.7.10.0", {"start": v(791.62, 460.02) * mm, "end": v(889.41, 460.02) * mm});
            skLineSegment(sketch, "E1.7.10.1", {"start": v(791.62, 453.16) * mm, "end": v(889.41, 453.16) * mm});
            skLineSegment(sketch, "E1.7.10.2", {"start": v(889.41, 460.02) * mm, "end": v(889.41, 453.16) * mm});
            skLineSegment(sketch, "E1.7.10.3", {"start": v(791.62, 460.02) * mm, "end": v(791.62, 453.16) * mm});
            skLineSegment(sketch, "E1.7.11.0", {"start": v(791.62, 499.39) * mm, "end": v(889.41, 499.39) * mm});
            skLineSegment(sketch, "E1.7.11.1", {"start": v(791.62, 492.53) * mm, "end": v(889.41, 492.53) * mm});
            skLineSegment(sketch, "E1.7.11.2", {"start": v(889.41, 499.39) * mm, "end": v(889.41, 492.53) * mm});
            skLineSegment(sketch, "E1.7.11.3", {"start": v(791.62, 499.39) * mm, "end": v(791.62, 492.53) * mm});
            skLineSegment(sketch, "E1.7.12.0", {"start": v(791.62, 538.76) * mm, "end": v(889.41, 538.76) * mm});
            skLineSegment(sketch, "E1.7.12.1", {"start": v(791.62, 531.9) * mm, "end": v(889.41, 531.9) * mm});
            skLineSegment(sketch, "E1.7.12.2", {"start": v(889.41, 538.76) * mm, "end": v(889.41, 531.9) * mm});
            skLineSegment(sketch, "E1.7.12.3", {"start": v(791.62, 538.76) * mm, "end": v(791.62, 531.9) * mm});
            skLineSegment(sketch, "E1.7.13.0", {"start": v(791.62, 578.13) * mm, "end": v(889.41, 578.13) * mm});
            skLineSegment(sketch, "E1.7.13.1", {"start": v(791.62, 571.27) * mm, "end": v(889.41, 571.27) * mm});
            skLineSegment(sketch, "E1.7.13.2", {"start": v(889.41, 578.13) * mm, "end": v(889.41, 571.27) * mm});
            skLineSegment(sketch, "E1.7.13.3", {"start": v(791.62, 578.13) * mm, "end": v(791.62, 571.27) * mm});
            skLineSegment(sketch, "E1.7.14.0", {"start": v(791.62, 617.5) * mm, "end": v(889.41, 617.5) * mm});
            skLineSegment(sketch, "E1.7.14.1", {"start": v(791.62, 610.64) * mm, "end": v(889.41, 610.64) * mm});
            skLineSegment(sketch, "E1.7.14.2", {"start": v(889.41, 617.5) * mm, "end": v(889.41, 610.64) * mm});
            skLineSegment(sketch, "E1.7.14.3", {"start": v(791.62, 617.5) * mm, "end": v(791.62, 610.64) * mm});
            skLineSegment(sketch, "E1.7.15.0", {"start": v(791.62, 656.87) * mm, "end": v(889.41, 656.87) * mm});
            skLineSegment(sketch, "E1.7.15.1", {"start": v(791.62, 650.01) * mm, "end": v(889.41, 650.01) * mm});
            skLineSegment(sketch, "E1.7.15.2", {"start": v(889.41, 656.87) * mm, "end": v(889.41, 650.01) * mm});
            skLineSegment(sketch, "E1.7.15.3", {"start": v(791.62, 656.87) * mm, "end": v(791.62, 650.01) * mm});
            skLineSegment(sketch, "E1.7.16.0", {"start": v(791.62, 696.24) * mm, "end": v(889.41, 696.24) * mm});
            skLineSegment(sketch, "E1.7.16.1", {"start": v(791.62, 689.38) * mm, "end": v(889.41, 689.38) * mm});
            skLineSegment(sketch, "E1.7.16.2", {"start": v(889.41, 696.24) * mm, "end": v(889.41, 689.38) * mm});
            skLineSegment(sketch, "E1.7.16.3", {"start": v(791.62, 696.24) * mm, "end": v(791.62, 689.38) * mm});
            skLineSegment(sketch, "E1.7.17.0", {"start": v(791.62, 735.6) * mm, "end": v(889.41, 735.6) * mm});
            skLineSegment(sketch, "E1.7.17.1", {"start": v(791.62, 728.75) * mm, "end": v(889.41, 728.75) * mm});
            skLineSegment(sketch, "E1.7.17.2", {"start": v(889.41, 735.6) * mm, "end": v(889.41, 728.75) * mm});
            skLineSegment(sketch, "E1.7.17.3", {"start": v(791.62, 735.6) * mm, "end": v(791.62, 728.75) * mm});
            skLineSegment(sketch, "E1.7.18.0", {"start": v(791.62, 774.98) * mm, "end": v(889.41, 774.98) * mm});
            skLineSegment(sketch, "E1.7.18.1", {"start": v(791.62, 768.12) * mm, "end": v(889.41, 768.12) * mm});
            skLineSegment(sketch, "E1.7.18.2", {"start": v(889.41, 774.98) * mm, "end": v(889.41, 768.12) * mm});
            skLineSegment(sketch, "E1.7.18.3", {"start": v(791.62, 774.98) * mm, "end": v(791.62, 768.12) * mm});
            skLineSegment(sketch, "E1.7.19.0", {"start": v(791.62, 814.35) * mm, "end": v(889.41, 814.35) * mm});
            skLineSegment(sketch, "E1.7.19.1", {"start": v(791.62, 807.5) * mm, "end": v(889.41, 807.5) * mm});
            skLineSegment(sketch, "E1.7.19.2", {"start": v(889.41, 814.35) * mm, "end": v(889.41, 807.5) * mm});
            skLineSegment(sketch, "E1.7.19.3", {"start": v(791.62, 814.35) * mm, "end": v(791.62, 807.5) * mm});
            skLineSegment(sketch, "E1.7.20.0", {"start": v(791.62, 853.72) * mm, "end": v(889.41, 853.72) * mm});
            skLineSegment(sketch, "E1.7.20.1", {"start": v(791.62, 846.86) * mm, "end": v(889.41, 846.86) * mm});
            skLineSegment(sketch, "E1.7.20.2", {"start": v(889.41, 853.72) * mm, "end": v(889.41, 846.86) * mm});
            skLineSegment(sketch, "E1.7.20.3", {"start": v(791.62, 853.72) * mm, "end": v(791.62, 846.86) * mm});
            skLineSegment(sketch, "E1.7.21.0", {"start": v(791.62, 893.09) * mm, "end": v(889.41, 893.09) * mm});
            skLineSegment(sketch, "E1.7.21.1", {"start": v(791.62, 886.23) * mm, "end": v(889.41, 886.23) * mm});
            skLineSegment(sketch, "E1.7.21.2", {"start": v(889.41, 893.09) * mm, "end": v(889.41, 886.23) * mm});
            skLineSegment(sketch, "E1.7.21.3", {"start": v(791.62, 893.09) * mm, "end": v(791.62, 886.23) * mm});
            skLineSegment(sketch, "E1.7.22.0", {"start": v(791.62, 932.46) * mm, "end": v(889.41, 932.46) * mm});
            skLineSegment(sketch, "E1.7.22.1", {"start": v(791.62, 925.6) * mm, "end": v(889.41, 925.6) * mm});
            skLineSegment(sketch, "E1.7.22.2", {"start": v(889.41, 932.46) * mm, "end": v(889.41, 925.6) * mm});
            skLineSegment(sketch, "E1.7.22.3", {"start": v(791.62, 932.46) * mm, "end": v(791.62, 925.6) * mm});
            skLineSegment(sketch, "E1.7.23.0", {"start": v(791.62, 971.83) * mm, "end": v(889.41, 971.83) * mm});
            skLineSegment(sketch, "E1.7.23.1", {"start": v(791.62, 964.97) * mm, "end": v(889.41, 964.97) * mm});
            skLineSegment(sketch, "E1.7.23.2", {"start": v(889.41, 971.83) * mm, "end": v(889.41, 964.97) * mm});
            skLineSegment(sketch, "E1.7.23.3", {"start": v(791.62, 971.83) * mm, "end": v(791.62, 964.97) * mm});
            skLineSegment(sketch, "E1.7.24.0", {"start": v(791.62, 1011.2) * mm, "end": v(889.41, 1011.2) * mm});
            skLineSegment(sketch, "E1.7.24.1", {"start": v(791.62, 1004.34) * mm, "end": v(889.41, 1004.34) * mm});
            skLineSegment(sketch, "E1.7.24.2", {"start": v(889.41, 1011.2) * mm, "end": v(889.41, 1004.34) * mm});
            skLineSegment(sketch, "E1.7.24.3", {"start": v(791.62, 1011.2) * mm, "end": v(791.62, 1004.34) * mm});
            skLineSegment(sketch, "E1.7.25.0", {"start": v(791.62, 1050.57) * mm, "end": v(889.41, 1050.57) * mm});
            skLineSegment(sketch, "E1.7.25.1", {"start": v(791.62, 1043.71) * mm, "end": v(889.41, 1043.71) * mm});
            skLineSegment(sketch, "E1.7.25.2", {"start": v(889.41, 1050.57) * mm, "end": v(889.41, 1043.71) * mm});
            skLineSegment(sketch, "E1.7.25.3", {"start": v(791.62, 1050.57) * mm, "end": v(791.62, 1043.71) * mm});
            skLineSegment(sketch, "E1.7.26.0", {"start": v(791.62, 1089.94) * mm, "end": v(889.41, 1089.94) * mm});
            skLineSegment(sketch, "E1.7.26.1", {"start": v(791.62, 1083.08) * mm, "end": v(889.41, 1083.08) * mm});
            skLineSegment(sketch, "E1.7.26.2", {"start": v(889.41, 1089.94) * mm, "end": v(889.41, 1083.08) * mm});
            skLineSegment(sketch, "E1.7.26.3", {"start": v(791.62, 1089.94) * mm, "end": v(791.62, 1083.08) * mm});
            skLineSegment(sketch, "E1.7.27.0", {"start": v(791.62, 1129.3) * mm, "end": v(889.41, 1129.3) * mm});
            skLineSegment(sketch, "E1.7.27.1", {"start": v(791.62, 1122.45) * mm, "end": v(889.41, 1122.45) * mm});
            skLineSegment(sketch, "E1.7.27.2", {"start": v(889.41, 1129.3) * mm, "end": v(889.41, 1122.45) * mm});
            skLineSegment(sketch, "E1.7.27.3", {"start": v(791.62, 1129.3) * mm, "end": v(791.62, 1122.45) * mm});
            skLineSegment(sketch, "E1.7.28.0", {"start": v(791.62, 1168.68) * mm, "end": v(889.41, 1168.68) * mm});
            skLineSegment(sketch, "E1.7.28.1", {"start": v(791.62, 1161.82) * mm, "end": v(889.41, 1161.82) * mm});
            skLineSegment(sketch, "E1.7.28.2", {"start": v(889.41, 1168.68) * mm, "end": v(889.41, 1161.82) * mm});
            skLineSegment(sketch, "E1.7.28.3", {"start": v(791.62, 1168.68) * mm, "end": v(791.62, 1161.82) * mm});
            skLineSegment(sketch, "E1.7.29.0", {"start": v(791.62, 1208.05) * mm, "end": v(889.41, 1208.05) * mm});
            skLineSegment(sketch, "E1.7.29.1", {"start": v(791.62, 1201.2) * mm, "end": v(889.41, 1201.2) * mm});
            skLineSegment(sketch, "E1.7.29.2", {"start": v(889.41, 1208.05) * mm, "end": v(889.41, 1201.2) * mm});
            skLineSegment(sketch, "E1.7.29.3", {"start": v(791.62, 1208.05) * mm, "end": v(791.62, 1201.2) * mm});
            skLineSegment(sketch, "E1.direction1", {"start": v(-104.49, 59.46) * mm, "end": v(23.53, 59.46) * mm, "construction": true});
            skLineSegment(sketch, "E1.direction2", {"start": v(-104.49, 59.46) * mm, "end": v(-104.49, 98.83) * mm, "construction": true});
            skSolve(sketch);
        }
        {
            var Q0;
            Q0 = qSketchRegion(id + "F0", true);
            extrude(context, id + "F1", {"entities" : qUnion([Q0]), "depth" : 8.9 * mm, "offsetDistance" : 25.4 * mm});
        }
    });
